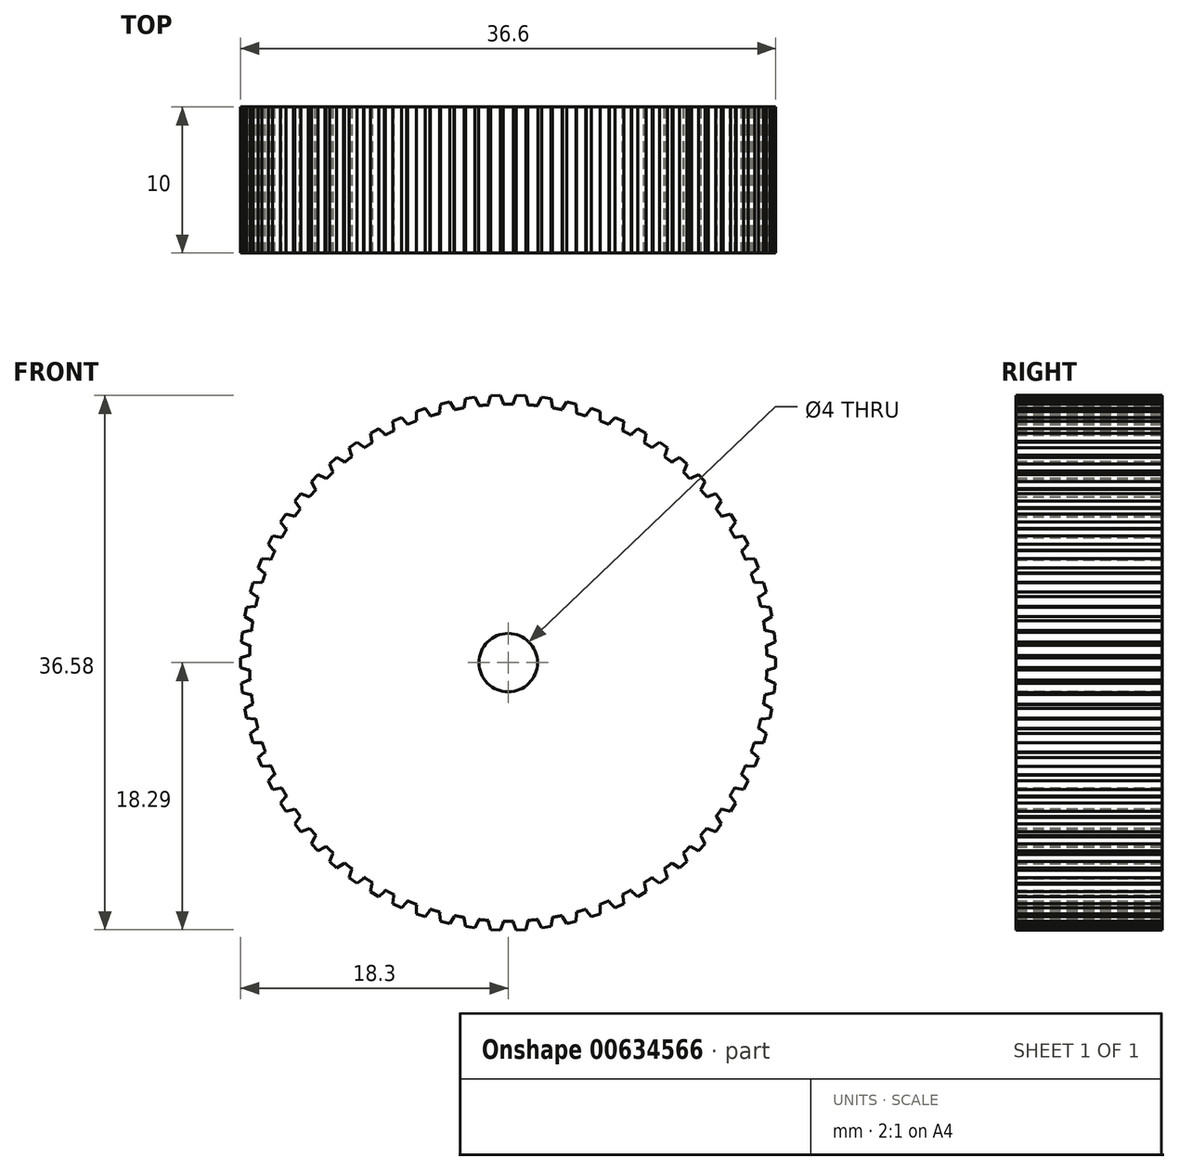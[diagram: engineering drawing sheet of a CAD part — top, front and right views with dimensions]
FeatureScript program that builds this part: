
annotation { "Feature Type Name" : "Feature", "Feature Type Description" : "" }
export const myFeature = defineFeature(function(context is Context, id is Id, definition is map)
    precondition{}
    {
        {
            var Q0;
            Q0=qCreatedBy(makeId("Front.planeOp"),FACE);
            var sketch = newSketch(context, id + "F0", { "sketchPlane" : qUnion([Q0])});
            skCircle(sketch, "E0", {"center": v(0, 0) * mm, "radius": 17.7 * mm});
            skLineSegment(sketch, "E1", {"start": v(0, 0) * mm, "end": v(17.7, 0) * mm, "construction": true});
            skLineSegment(sketch, "E2", {"start": v(17.7, 0) * mm, "end": v(18.3, 0) * mm, "construction": true});
            skLineSegment(sketch, "E3", {"start": v(18.3, 0) * mm, "end": v(18.3, 0.33) * mm});
            skLineSegment(sketch, "E4", {"start": v(17.7, 0.5) * mm, "end": v(17.8, 0.5) * mm});
            skLineSegment(sketch, "E5", {"start": v(17.8, 0.5) * mm, "end": v(18.3, 0.33) * mm});
            skLineSegment(sketch, "E6.MirrorCS", {"start": v(17.8, -0.5) * mm, "end": v(18.3, -0.33) * mm});
            skLineSegment(sketch, "E7.MirrorCS", {"start": v(18.3, 0) * mm, "end": v(18.3, -0.33) * mm});
            skLineSegment(sketch, "E8.MirrorCS", {"start": v(17.7, -0.5) * mm, "end": v(17.8, -0.5) * mm});
            skLineSegment(sketch, "E9.1.0", {"start": v(-28.82, -3.03) * mm, "end": v(-28.73, -3) * mm});
            skLineSegment(sketch, "E9.1.1", {"start": v(-28.73, -3) * mm, "end": v(-28.2, -3.01) * mm});
            skLineSegment(sketch, "E9.1.2", {"start": v(-28.1, -3.33) * mm, "end": v(-28.2, -3.01) * mm});
            skLineSegment(sketch, "E9.1.3", {"start": v(-28.1, -3.33) * mm, "end": v(-28, -3.64) * mm});
            skLineSegment(sketch, "E9.1.4", {"start": v(-28.43, -3.96) * mm, "end": v(-28, -3.64) * mm});
            skLineSegment(sketch, "E9.1.5", {"start": v(-28.53, -3.99) * mm, "end": v(-28.43, -3.96) * mm});
            skLineSegment(sketch, "E9.2.0", {"start": v(-72.23, -20.11) * mm, "end": v(-72.15, -20.06) * mm});
            skLineSegment(sketch, "E9.2.1", {"start": v(-72.15, -20.06) * mm, "end": v(-71.63, -19.91) * mm});
            skLineSegment(sketch, "E9.2.2", {"start": v(-71.45, -20.19) * mm, "end": v(-71.63, -19.91) * mm});
            skLineSegment(sketch, "E9.2.3", {"start": v(-71.45, -20.19) * mm, "end": v(-71.26, -20.46) * mm});
            skLineSegment(sketch, "E9.2.4", {"start": v(-71.58, -20.88) * mm, "end": v(-71.26, -20.46) * mm});
            skLineSegment(sketch, "E9.2.5", {"start": v(-71.67, -20.94) * mm, "end": v(-71.58, -20.88) * mm});
            skLineSegment(sketch, "E9.3.0", {"start": v(-108.67, -49.23) * mm, "end": v(-108.6, -49.15) * mm});
            skLineSegment(sketch, "E9.3.1", {"start": v(-108.6, -49.15) * mm, "end": v(-108.16, -48.86) * mm});
            skLineSegment(sketch, "E9.3.2", {"start": v(-107.9, -49.07) * mm, "end": v(-108.16, -48.86) * mm});
            skLineSegment(sketch, "E9.3.3", {"start": v(-107.9, -49.07) * mm, "end": v(-107.64, -49.28) * mm});
            skLineSegment(sketch, "E9.3.4", {"start": v(-107.83, -49.78) * mm, "end": v(-107.64, -49.28) * mm});
            skLineSegment(sketch, "E9.3.5", {"start": v(-107.89, -49.86) * mm, "end": v(-107.83, -49.78) * mm});
            skLineSegment(sketch, "E9.4.0", {"start": v(-134.91, -87.8) * mm, "end": v(-134.88, -87.7) * mm});
            skLineSegment(sketch, "E9.4.1", {"start": v(-134.88, -87.7) * mm, "end": v(-134.53, -87.3) * mm});
            skLineSegment(sketch, "E9.4.2", {"start": v(-134.23, -87.42) * mm, "end": v(-134.53, -87.3) * mm});
            skLineSegment(sketch, "E9.4.3", {"start": v(-134.23, -87.42) * mm, "end": v(-133.92, -87.54) * mm});
            skLineSegment(sketch, "E9.4.4", {"start": v(-133.95, -88.07) * mm, "end": v(-133.92, -87.54) * mm});
            skLineSegment(sketch, "E9.4.5", {"start": v(-133.98, -88.17) * mm, "end": v(-133.95, -88.07) * mm});
            skLineSegment(sketch, "E9.5.0", {"start": v(-148.62, -132.39) * mm, "end": v(-148.61, -132.29) * mm});
            skLineSegment(sketch, "E9.5.1", {"start": v(-148.61, -132.29) * mm, "end": v(-148.4, -131.8) * mm});
            skLineSegment(sketch, "E9.5.2", {"start": v(-148.08, -131.82) * mm, "end": v(-148.4, -131.8) * mm});
            skLineSegment(sketch, "E9.5.3", {"start": v(-148.08, -131.82) * mm, "end": v(-147.75, -131.85) * mm});
            skLineSegment(sketch, "E9.5.4", {"start": v(-147.62, -132.36) * mm, "end": v(-147.75, -131.85) * mm});
            skLineSegment(sketch, "E9.5.5", {"start": v(-147.62, -132.46) * mm, "end": v(-147.62, -132.36) * mm});
            skLineSegment(sketch, "E9.6.0", {"start": v(-148.58, -179.04) * mm, "end": v(-148.6, -178.94) * mm});
            skLineSegment(sketch, "E9.6.1", {"start": v(-148.6, -178.94) * mm, "end": v(-148.54, -178.4) * mm});
            skLineSegment(sketch, "E9.6.2", {"start": v(-148.22, -178.33) * mm, "end": v(-148.54, -178.4) * mm});
            skLineSegment(sketch, "E9.6.3", {"start": v(-148.22, -178.33) * mm, "end": v(-147.9, -178.26) * mm});
            skLineSegment(sketch, "E9.6.4", {"start": v(-147.62, -178.72) * mm, "end": v(-147.9, -178.26) * mm});
            skLineSegment(sketch, "E9.6.5", {"start": v(-147.6, -178.81) * mm, "end": v(-147.62, -178.72) * mm});
            skLineSegment(sketch, "E9.7.0", {"start": v(-134.78, -223.6) * mm, "end": v(-134.83, -223.51) * mm});
            skLineSegment(sketch, "E9.7.1", {"start": v(-134.83, -223.51) * mm, "end": v(-134.94, -222.99) * mm});
            skLineSegment(sketch, "E9.7.2", {"start": v(-134.65, -222.82) * mm, "end": v(-134.94, -222.99) * mm});
            skLineSegment(sketch, "E9.7.3", {"start": v(-134.65, -222.82) * mm, "end": v(-134.37, -222.66) * mm});
            skLineSegment(sketch, "E9.7.4", {"start": v(-133.97, -223.01) * mm, "end": v(-134.37, -222.66) * mm});
            skLineSegment(sketch, "E9.7.5", {"start": v(-133.92, -223.1) * mm, "end": v(-133.97, -223.01) * mm});
            skLineSegment(sketch, "E9.8.0", {"start": v(-108.47, -262.12) * mm, "end": v(-108.54, -262.05) * mm});
            skLineSegment(sketch, "E9.8.1", {"start": v(-108.54, -262.05) * mm, "end": v(-108.8, -261.58) * mm});
            skLineSegment(sketch, "E9.8.2", {"start": v(-108.57, -261.34) * mm, "end": v(-108.8, -261.58) * mm});
            skLineSegment(sketch, "E9.8.3", {"start": v(-108.57, -261.34) * mm, "end": v(-108.35, -261.1) * mm});
            skLineSegment(sketch, "E9.8.4", {"start": v(-107.86, -261.32) * mm, "end": v(-108.35, -261.1) * mm});
            skLineSegment(sketch, "E9.8.5", {"start": v(-107.79, -261.38) * mm, "end": v(-107.86, -261.32) * mm});
            skLineSegment(sketch, "E9.9.0", {"start": v(-71.97, -291.17) * mm, "end": v(-72.06, -291.12) * mm});
            skLineSegment(sketch, "E9.9.1", {"start": v(-72.06, -291.12) * mm, "end": v(-72.44, -290.75) * mm});
            skLineSegment(sketch, "E9.9.2", {"start": v(-72.3, -290.45) * mm, "end": v(-72.44, -290.75) * mm});
            skLineSegment(sketch, "E9.9.3", {"start": v(-72.3, -290.45) * mm, "end": v(-72.16, -290.16) * mm});
            skLineSegment(sketch, "E9.9.4", {"start": v(-71.63, -290.22) * mm, "end": v(-72.16, -290.16) * mm});
            skLineSegment(sketch, "E9.9.5", {"start": v(-71.54, -290.27) * mm, "end": v(-71.63, -290.22) * mm});
            skLineSegment(sketch, "E9.10.0", {"start": v(-28.53, -308.17) * mm, "end": v(-28.63, -308.15) * mm});
            skLineSegment(sketch, "E9.10.1", {"start": v(-28.63, -308.15) * mm, "end": v(-29.1, -307.9) * mm});
            skLineSegment(sketch, "E9.10.2", {"start": v(-29.06, -307.58) * mm, "end": v(-29.1, -307.9) * mm});
            skLineSegment(sketch, "E9.10.3", {"start": v(-29.06, -307.58) * mm, "end": v(-29, -307.26) * mm});
            skLineSegment(sketch, "E9.10.4", {"start": v(-28.48, -307.16) * mm, "end": v(-29, -307.26) * mm});
            skLineSegment(sketch, "E9.10.5", {"start": v(-28.38, -307.18) * mm, "end": v(-28.48, -307.16) * mm});
            skLineSegment(sketch, "E9.11.0", {"start": v(17.99, -311.6) * mm, "end": v(17.9, -311.62) * mm});
            skLineSegment(sketch, "E9.11.1", {"start": v(17.9, -311.62) * mm, "end": v(17.36, -311.53) * mm});
            skLineSegment(sketch, "E9.11.2", {"start": v(17.31, -311.2) * mm, "end": v(17.36, -311.53) * mm});
            skLineSegment(sketch, "E9.11.3", {"start": v(17.31, -311.2) * mm, "end": v(17.27, -310.88) * mm});
            skLineSegment(sketch, "E9.11.4", {"start": v(17.74, -310.64) * mm, "end": v(17.27, -310.88) * mm});
            skLineSegment(sketch, "E9.11.5", {"start": v(17.84, -310.62) * mm, "end": v(17.74, -310.64) * mm});
            skLineSegment(sketch, "E9.12.0", {"start": v(63.46, -301.19) * mm, "end": v(63.37, -301.23) * mm});
            skLineSegment(sketch, "E9.12.1", {"start": v(63.37, -301.23) * mm, "end": v(62.84, -301.3) * mm});
            skLineSegment(sketch, "E9.12.2", {"start": v(62.7, -301) * mm, "end": v(62.84, -301.3) * mm});
            skLineSegment(sketch, "E9.12.3", {"start": v(62.7, -301) * mm, "end": v(62.55, -300.7) * mm});
            skLineSegment(sketch, "E9.12.4", {"start": v(62.93, -300.33) * mm, "end": v(62.55, -300.7) * mm});
            skLineSegment(sketch, "E9.12.5", {"start": v(63.02, -300.28) * mm, "end": v(62.93, -300.33) * mm});
            skLineSegment(sketch, "E9.13.0", {"start": v(103.83, -277.82) * mm, "end": v(103.76, -277.9) * mm});
            skLineSegment(sketch, "E9.13.1", {"start": v(103.76, -277.9) * mm, "end": v(103.27, -278.11) * mm});
            skLineSegment(sketch, "E9.13.2", {"start": v(103.05, -277.87) * mm, "end": v(103.27, -278.11) * mm});
            skLineSegment(sketch, "E9.13.3", {"start": v(103.05, -277.87) * mm, "end": v(102.82, -277.63) * mm});
            skLineSegment(sketch, "E9.13.4", {"start": v(103.08, -277.16) * mm, "end": v(102.82, -277.63) * mm});
            skLineSegment(sketch, "E9.13.5", {"start": v(103.15, -277.1) * mm, "end": v(103.08, -277.16) * mm});
            skLineSegment(sketch, "E9.14.0", {"start": v(135.53, -243.6) * mm, "end": v(135.48, -243.68) * mm});
            skLineSegment(sketch, "E9.14.1", {"start": v(135.48, -243.68) * mm, "end": v(135.08, -244.04) * mm});
            skLineSegment(sketch, "E9.14.2", {"start": v(134.8, -243.87) * mm, "end": v(135.08, -244.04) * mm});
            skLineSegment(sketch, "E9.14.3", {"start": v(134.8, -243.87) * mm, "end": v(134.5, -243.7) * mm});
            skLineSegment(sketch, "E9.14.4", {"start": v(134.61, -243.18) * mm, "end": v(134.5, -243.7) * mm});
            skLineSegment(sketch, "E9.14.5", {"start": v(134.66, -243.1) * mm, "end": v(134.61, -243.18) * mm});
            skLineSegment(sketch, "E9.15.0", {"start": v(155.73, -201.55) * mm, "end": v(155.7, -201.65) * mm});
            skLineSegment(sketch, "E9.15.1", {"start": v(155.7, -201.65) * mm, "end": v(155.43, -202.1) * mm});
            skLineSegment(sketch, "E9.15.2", {"start": v(155.1, -202.03) * mm, "end": v(155.43, -202.1) * mm});
            skLineSegment(sketch, "E9.15.3", {"start": v(155.1, -202.03) * mm, "end": v(154.79, -201.96) * mm});
            skLineSegment(sketch, "E9.15.4", {"start": v(154.73, -201.43) * mm, "end": v(154.79, -201.96) * mm});
            skLineSegment(sketch, "E9.15.5", {"start": v(154.76, -201.33) * mm, "end": v(154.73, -201.43) * mm});
            skLineSegment(sketch, "E9.16.0", {"start": v(162.64, -155.42) * mm, "end": v(162.65, -155.52) * mm});
            skLineSegment(sketch, "E9.16.1", {"start": v(162.65, -155.52) * mm, "end": v(162.51, -156.04) * mm});
            skLineSegment(sketch, "E9.16.2", {"start": v(162.19, -156.06) * mm, "end": v(162.51, -156.04) * mm});
            skLineSegment(sketch, "E9.16.3", {"start": v(162.19, -156.06) * mm, "end": v(161.86, -156.08) * mm});
            skLineSegment(sketch, "E9.16.4", {"start": v(161.65, -155.6) * mm, "end": v(161.86, -156.08) * mm});
            skLineSegment(sketch, "E9.16.5", {"start": v(161.64, -155.5) * mm, "end": v(161.65, -155.6) * mm});
            skLineSegment(sketch, "E9.17.0", {"start": v(155.64, -109.3) * mm, "end": v(155.68, -109.39) * mm});
            skLineSegment(sketch, "E9.17.1", {"start": v(155.68, -109.39) * mm, "end": v(155.7, -109.92) * mm});
            skLineSegment(sketch, "E9.17.2", {"start": v(155.4, -110.04) * mm, "end": v(155.7, -109.92) * mm});
            skLineSegment(sketch, "E9.17.3", {"start": v(155.4, -110.04) * mm, "end": v(155.1, -110.17) * mm});
            skLineSegment(sketch, "E9.17.4", {"start": v(154.75, -109.76) * mm, "end": v(155.1, -110.17) * mm});
            skLineSegment(sketch, "E9.17.5", {"start": v(154.71, -109.66) * mm, "end": v(154.75, -109.76) * mm});
            skLineSegment(sketch, "E9.18.0", {"start": v(135.36, -67.29) * mm, "end": v(135.43, -67.37) * mm});
            skLineSegment(sketch, "E9.18.1", {"start": v(135.43, -67.37) * mm, "end": v(135.6, -67.87) * mm});
            skLineSegment(sketch, "E9.18.2", {"start": v(135.35, -68.07) * mm, "end": v(135.6, -67.87) * mm});
            skLineSegment(sketch, "E9.18.3", {"start": v(135.35, -68.07) * mm, "end": v(135.1, -68.28) * mm});
            skLineSegment(sketch, "E9.18.4", {"start": v(134.64, -67.99) * mm, "end": v(135.1, -68.28) * mm});
            skLineSegment(sketch, "E9.18.5", {"start": v(134.58, -67.91) * mm, "end": v(134.64, -67.99) * mm});
            skLineSegment(sketch, "E9.19.0", {"start": v(103.6, -33.12) * mm, "end": v(103.68, -33.18) * mm});
            skLineSegment(sketch, "E9.19.1", {"start": v(103.68, -33.18) * mm, "end": v(104, -33.6) * mm});
            skLineSegment(sketch, "E9.19.2", {"start": v(103.82, -33.88) * mm, "end": v(104, -33.6) * mm});
            skLineSegment(sketch, "E9.19.3", {"start": v(103.82, -33.88) * mm, "end": v(103.64, -34.15) * mm});
            skLineSegment(sketch, "E9.19.4", {"start": v(103.12, -34) * mm, "end": v(103.64, -34.15) * mm});
            skLineSegment(sketch, "E9.19.5", {"start": v(103.04, -33.95) * mm, "end": v(103.12, -34) * mm});
            skLineSegment(sketch, "E9.20.0", {"start": v(63.18, -9.84) * mm, "end": v(63.28, -9.87) * mm});
            skLineSegment(sketch, "E9.20.1", {"start": v(63.28, -9.87) * mm, "end": v(63.71, -10.18) * mm});
            skLineSegment(sketch, "E9.20.2", {"start": v(63.61, -10.5) * mm, "end": v(63.71, -10.18) * mm});
            skLineSegment(sketch, "E9.20.3", {"start": v(63.61, -10.5) * mm, "end": v(63.52, -10.8) * mm});
            skLineSegment(sketch, "E9.20.4", {"start": v(62.98, -10.82) * mm, "end": v(63.52, -10.8) * mm});
            skLineSegment(sketch, "E9.20.5", {"start": v(62.89, -10.8) * mm, "end": v(62.98, -10.82) * mm});
            skLineSegment(sketch, "E10.1.0", {"start": v(17.57, 2.18) * mm, "end": v(17.66, 2.19) * mm});
            skLineSegment(sketch, "E10.1.1", {"start": v(17.66, 2.19) * mm, "end": v(18.19, 2.07) * mm});
            skLineSegment(sketch, "E10.1.2", {"start": v(18.22, 1.74) * mm, "end": v(18.25, 1.41) * mm});
            skLineSegment(sketch, "E10.1.3", {"start": v(18.22, 1.74) * mm, "end": v(18.19, 2.07) * mm});
            skLineSegment(sketch, "E10.1.4", {"start": v(17.76, 1.2) * mm, "end": v(18.25, 1.41) * mm});
            skLineSegment(sketch, "E10.1.5", {"start": v(17.66, 1.18) * mm, "end": v(17.76, 1.2) * mm});
            skLineSegment(sketch, "E10.2.0", {"start": v(17.28, 3.84) * mm, "end": v(17.38, 3.86) * mm});
            skLineSegment(sketch, "E10.2.1", {"start": v(17.38, 3.86) * mm, "end": v(17.9, 3.79) * mm});
            skLineSegment(sketch, "E10.2.2", {"start": v(17.97, 3.46) * mm, "end": v(18.03, 3.14) * mm});
            skLineSegment(sketch, "E10.2.3", {"start": v(17.97, 3.46) * mm, "end": v(17.9, 3.79) * mm});
            skLineSegment(sketch, "E10.2.4", {"start": v(17.57, 2.88) * mm, "end": v(18.03, 3.14) * mm});
            skLineSegment(sketch, "E10.2.5", {"start": v(17.47, 2.86) * mm, "end": v(17.57, 2.88) * mm});
            skLineSegment(sketch, "E10.3.0", {"start": v(16.84, 5.46) * mm, "end": v(16.93, 5.5) * mm});
            skLineSegment(sketch, "E10.3.1", {"start": v(16.93, 5.5) * mm, "end": v(17.47, 5.47) * mm});
            skLineSegment(sketch, "E10.3.2", {"start": v(17.56, 5.16) * mm, "end": v(17.65, 4.84) * mm});
            skLineSegment(sketch, "E10.3.3", {"start": v(17.56, 5.16) * mm, "end": v(17.47, 5.47) * mm});
            skLineSegment(sketch, "E10.3.4", {"start": v(17.21, 4.53) * mm, "end": v(17.65, 4.84) * mm});
            skLineSegment(sketch, "E10.3.5", {"start": v(17.12, 4.5) * mm, "end": v(17.21, 4.53) * mm});
            skLineSegment(sketch, "E10.4.0", {"start": v(16.24, 7.04) * mm, "end": v(16.33, 7.08) * mm});
            skLineSegment(sketch, "E10.4.1", {"start": v(16.33, 7.08) * mm, "end": v(16.87, 7.1) * mm});
            skLineSegment(sketch, "E10.4.2", {"start": v(16.99, 6.8) * mm, "end": v(17.11, 6.5) * mm});
            skLineSegment(sketch, "E10.4.3", {"start": v(16.99, 6.8) * mm, "end": v(16.87, 7.1) * mm});
            skLineSegment(sketch, "E10.4.4", {"start": v(16.7, 6.15) * mm, "end": v(17.11, 6.5) * mm});
            skLineSegment(sketch, "E10.4.5", {"start": v(16.61, 6.11) * mm, "end": v(16.7, 6.15) * mm});
            skLineSegment(sketch, "E10.5.0", {"start": v(15.5, 8.55) * mm, "end": v(15.59, 8.6) * mm});
            skLineSegment(sketch, "E10.5.1", {"start": v(15.59, 8.6) * mm, "end": v(16.11, 8.68) * mm});
            skLineSegment(sketch, "E10.5.2", {"start": v(16.27, 8.39) * mm, "end": v(16.42, 8.1) * mm});
            skLineSegment(sketch, "E10.5.3", {"start": v(16.27, 8.39) * mm, "end": v(16.11, 8.68) * mm});
            skLineSegment(sketch, "E10.5.4", {"start": v(16.04, 7.7) * mm, "end": v(16.42, 8.1) * mm});
            skLineSegment(sketch, "E10.5.5", {"start": v(15.96, 7.66) * mm, "end": v(16.04, 7.7) * mm});
            skLineSegment(sketch, "E10.6.0", {"start": v(14.61, 9.99) * mm, "end": v(14.7, 10.04) * mm});
            skLineSegment(sketch, "E10.6.1", {"start": v(14.7, 10.04) * mm, "end": v(15.22, 10.17) * mm});
            skLineSegment(sketch, "E10.6.2", {"start": v(15.4, 9.9) * mm, "end": v(15.57, 9.62) * mm});
            skLineSegment(sketch, "E10.6.3", {"start": v(15.4, 9.9) * mm, "end": v(15.22, 10.17) * mm});
            skLineSegment(sketch, "E10.6.4", {"start": v(15.24, 9.2) * mm, "end": v(15.57, 9.62) * mm});
            skLineSegment(sketch, "E10.6.5", {"start": v(15.15, 9.14) * mm, "end": v(15.24, 9.2) * mm});
            skLineSegment(sketch, "E10.7.0", {"start": v(13.6, 11.33) * mm, "end": v(13.68, 11.4) * mm});
            skLineSegment(sketch, "E10.7.1", {"start": v(13.68, 11.4) * mm, "end": v(14.18, 11.57) * mm});
            skLineSegment(sketch, "E10.7.2", {"start": v(14.38, 11.31) * mm, "end": v(14.59, 11.05) * mm});
            skLineSegment(sketch, "E10.7.3", {"start": v(14.38, 11.31) * mm, "end": v(14.18, 11.57) * mm});
            skLineSegment(sketch, "E10.7.4", {"start": v(14.3, 10.6) * mm, "end": v(14.59, 11.05) * mm});
            skLineSegment(sketch, "E10.7.5", {"start": v(14.22, 10.54) * mm, "end": v(14.3, 10.6) * mm});
            skLineSegment(sketch, "E10.8.0", {"start": v(12.46, 12.57) * mm, "end": v(12.53, 12.64) * mm});
            skLineSegment(sketch, "E10.8.1", {"start": v(12.53, 12.64) * mm, "end": v(13.02, 12.87) * mm});
            skLineSegment(sketch, "E10.8.2", {"start": v(13.24, 12.63) * mm, "end": v(13.47, 12.39) * mm});
            skLineSegment(sketch, "E10.8.3", {"start": v(13.24, 12.63) * mm, "end": v(13.02, 12.87) * mm});
            skLineSegment(sketch, "E10.8.4", {"start": v(13.22, 11.92) * mm, "end": v(13.47, 12.39) * mm});
            skLineSegment(sketch, "E10.8.5", {"start": v(13.15, 11.85) * mm, "end": v(13.22, 11.92) * mm});
            skLineSegment(sketch, "E10.9.0", {"start": v(11.2, 13.7) * mm, "end": v(11.27, 13.77) * mm});
            skLineSegment(sketch, "E10.9.1", {"start": v(11.27, 13.77) * mm, "end": v(11.73, 14.05) * mm});
            skLineSegment(sketch, "E10.9.2", {"start": v(11.98, 13.83) * mm, "end": v(12.23, 13.61) * mm});
            skLineSegment(sketch, "E10.9.3", {"start": v(11.98, 13.83) * mm, "end": v(11.73, 14.05) * mm});
            skLineSegment(sketch, "E10.9.4", {"start": v(12.03, 13.12) * mm, "end": v(12.23, 13.61) * mm});
            skLineSegment(sketch, "E10.9.5", {"start": v(11.96, 13.04) * mm, "end": v(12.03, 13.12) * mm});
            skLineSegment(sketch, "E10.10.0", {"start": v(9.86, 14.7) * mm, "end": v(9.91, 14.78) * mm});
            skLineSegment(sketch, "E10.10.1", {"start": v(9.91, 14.78) * mm, "end": v(10.35, 15.1) * mm});
            skLineSegment(sketch, "E10.10.2", {"start": v(10.62, 14.9) * mm, "end": v(10.88, 14.72) * mm});
            skLineSegment(sketch, "E10.10.3", {"start": v(10.62, 14.9) * mm, "end": v(10.35, 15.1) * mm});
            skLineSegment(sketch, "E10.10.4", {"start": v(10.73, 14.2) * mm, "end": v(10.88, 14.72) * mm});
            skLineSegment(sketch, "E10.10.5", {"start": v(10.67, 14.12) * mm, "end": v(10.73, 14.2) * mm});
            skLineSegment(sketch, "E10.11.0", {"start": v(8.41, 15.57) * mm, "end": v(8.46, 15.66) * mm});
            skLineSegment(sketch, "E10.11.1", {"start": v(8.46, 15.66) * mm, "end": v(8.86, 16.01) * mm});
            skLineSegment(sketch, "E10.11.2", {"start": v(9.15, 15.85) * mm, "end": v(9.44, 15.68) * mm});
            skLineSegment(sketch, "E10.11.3", {"start": v(9.15, 15.85) * mm, "end": v(8.86, 16.01) * mm});
            skLineSegment(sketch, "E10.11.4", {"start": v(9.33, 15.16) * mm, "end": v(9.44, 15.68) * mm});
            skLineSegment(sketch, "E10.11.5", {"start": v(9.28, 15.07) * mm, "end": v(9.33, 15.16) * mm});
            skLineSegment(sketch, "E10.12.0", {"start": v(6.9, 16.3) * mm, "end": v(6.94, 16.4) * mm});
            skLineSegment(sketch, "E10.12.1", {"start": v(6.94, 16.4) * mm, "end": v(7.3, 16.78) * mm});
            skLineSegment(sketch, "E10.12.2", {"start": v(7.6, 16.65) * mm, "end": v(7.9, 16.5) * mm});
            skLineSegment(sketch, "E10.12.3", {"start": v(7.6, 16.65) * mm, "end": v(7.3, 16.78) * mm});
            skLineSegment(sketch, "E10.12.4", {"start": v(7.85, 15.98) * mm, "end": v(7.9, 16.5) * mm});
            skLineSegment(sketch, "E10.12.5", {"start": v(7.8, 15.89) * mm, "end": v(7.85, 15.98) * mm});
            skLineSegment(sketch, "E10.13.0", {"start": v(5.31, 16.88) * mm, "end": v(5.35, 16.98) * mm});
            skLineSegment(sketch, "E10.13.1", {"start": v(5.35, 16.98) * mm, "end": v(5.67, 17.4) * mm});
            skLineSegment(sketch, "E10.13.2", {"start": v(5.99, 17.3) * mm, "end": v(6.3, 17.19) * mm});
            skLineSegment(sketch, "E10.13.3", {"start": v(5.99, 17.3) * mm, "end": v(5.67, 17.4) * mm});
            skLineSegment(sketch, "E10.13.4", {"start": v(6.3, 16.65) * mm, "end": v(6.3, 17.19) * mm});
            skLineSegment(sketch, "E10.13.5", {"start": v(6.26, 16.56) * mm, "end": v(6.3, 16.65) * mm});
            skLineSegment(sketch, "E10.14.0", {"start": v(3.69, 17.31) * mm, "end": v(3.7, 17.4) * mm});
            skLineSegment(sketch, "E10.14.1", {"start": v(3.7, 17.4) * mm, "end": v(4, 17.86) * mm});
            skLineSegment(sketch, "E10.14.2", {"start": v(4.31, 17.78) * mm, "end": v(4.64, 17.7) * mm});
            skLineSegment(sketch, "E10.14.3", {"start": v(4.31, 17.78) * mm, "end": v(4, 17.86) * mm});
            skLineSegment(sketch, "E10.14.4", {"start": v(4.68, 17.17) * mm, "end": v(4.64, 17.7) * mm});
            skLineSegment(sketch, "E10.14.5", {"start": v(4.66, 17.08) * mm, "end": v(4.68, 17.17) * mm});
            skLineSegment(sketch, "E10.15.0", {"start": v(2.02, 17.58) * mm, "end": v(2.04, 17.68) * mm});
            skLineSegment(sketch, "E10.15.1", {"start": v(2.04, 17.68) * mm, "end": v(2.28, 18.16) * mm});
            skLineSegment(sketch, "E10.15.2", {"start": v(2.6, 18.11) * mm, "end": v(2.93, 18.07) * mm});
            skLineSegment(sketch, "E10.15.3", {"start": v(2.6, 18.11) * mm, "end": v(2.28, 18.16) * mm});
            skLineSegment(sketch, "E10.15.4", {"start": v(3.03, 17.54) * mm, "end": v(2.93, 18.07) * mm});
            skLineSegment(sketch, "E10.15.5", {"start": v(3.01, 17.44) * mm, "end": v(3.03, 17.54) * mm});
            skLineSegment(sketch, "E10.16.0", {"start": v(0.34, 17.7) * mm, "end": v(0.35, 17.8) * mm});
            skLineSegment(sketch, "E10.16.1", {"start": v(0.35, 17.8) * mm, "end": v(0.54, 18.3) * mm});
            skLineSegment(sketch, "E10.16.2", {"start": v(0.87, 18.28) * mm, "end": v(1.2, 18.26) * mm});
            skLineSegment(sketch, "E10.16.3", {"start": v(0.87, 18.28) * mm, "end": v(0.54, 18.3) * mm});
            skLineSegment(sketch, "E10.16.4", {"start": v(1.35, 17.75) * mm, "end": v(1.2, 18.26) * mm});
            skLineSegment(sketch, "E10.16.5", {"start": v(1.34, 17.65) * mm, "end": v(1.35, 17.75) * mm});
            skLineSegment(sketch, "E10.17.0", {"start": v(-1.34, 17.65) * mm, "end": v(-1.35, 17.75) * mm});
            skLineSegment(sketch, "E10.17.1", {"start": v(-1.35, 17.75) * mm, "end": v(-1.2, 18.26) * mm});
            skLineSegment(sketch, "E10.17.2", {"start": v(-0.87, 18.28) * mm, "end": v(-0.54, 18.3) * mm});
            skLineSegment(sketch, "E10.17.3", {"start": v(-0.87, 18.28) * mm, "end": v(-1.2, 18.26) * mm});
            skLineSegment(sketch, "E10.17.4", {"start": v(-0.35, 17.8) * mm, "end": v(-0.54, 18.3) * mm});
            skLineSegment(sketch, "E10.17.5", {"start": v(-0.34, 17.7) * mm, "end": v(-0.35, 17.8) * mm});
            skLineSegment(sketch, "E10.18.0", {"start": v(-3.01, 17.44) * mm, "end": v(-3.03, 17.54) * mm});
            skLineSegment(sketch, "E10.18.1", {"start": v(-3.03, 17.54) * mm, "end": v(-2.93, 18.07) * mm});
            skLineSegment(sketch, "E10.18.2", {"start": v(-2.6, 18.11) * mm, "end": v(-2.28, 18.16) * mm});
            skLineSegment(sketch, "E10.18.3", {"start": v(-2.6, 18.11) * mm, "end": v(-2.93, 18.07) * mm});
            skLineSegment(sketch, "E10.18.4", {"start": v(-2.04, 17.68) * mm, "end": v(-2.28, 18.16) * mm});
            skLineSegment(sketch, "E10.18.5", {"start": v(-2.02, 17.58) * mm, "end": v(-2.04, 17.68) * mm});
            skLineSegment(sketch, "E10.19.0", {"start": v(-4.66, 17.08) * mm, "end": v(-4.68, 17.17) * mm});
            skLineSegment(sketch, "E10.19.1", {"start": v(-4.68, 17.17) * mm, "end": v(-4.64, 17.7) * mm});
            skLineSegment(sketch, "E10.19.2", {"start": v(-4.31, 17.78) * mm, "end": v(-4, 17.86) * mm});
            skLineSegment(sketch, "E10.19.3", {"start": v(-4.31, 17.78) * mm, "end": v(-4.64, 17.7) * mm});
            skLineSegment(sketch, "E10.19.4", {"start": v(-3.7, 17.4) * mm, "end": v(-4, 17.86) * mm});
            skLineSegment(sketch, "E10.19.5", {"start": v(-3.69, 17.31) * mm, "end": v(-3.7, 17.4) * mm});
            skLineSegment(sketch, "E10.20.0", {"start": v(-6.26, 16.56) * mm, "end": v(-6.3, 16.65) * mm});
            skLineSegment(sketch, "E10.20.1", {"start": v(-6.3, 16.65) * mm, "end": v(-6.3, 17.19) * mm});
            skLineSegment(sketch, "E10.20.2", {"start": v(-5.99, 17.3) * mm, "end": v(-5.67, 17.4) * mm});
            skLineSegment(sketch, "E10.20.3", {"start": v(-5.99, 17.3) * mm, "end": v(-6.3, 17.19) * mm});
            skLineSegment(sketch, "E10.20.4", {"start": v(-5.35, 16.98) * mm, "end": v(-5.67, 17.4) * mm});
            skLineSegment(sketch, "E10.20.5", {"start": v(-5.31, 16.88) * mm, "end": v(-5.35, 16.98) * mm});
            skLineSegment(sketch, "E10.21.0", {"start": v(-7.8, 15.89) * mm, "end": v(-7.85, 15.98) * mm});
            skLineSegment(sketch, "E10.21.1", {"start": v(-7.85, 15.98) * mm, "end": v(-7.9, 16.5) * mm});
            skLineSegment(sketch, "E10.21.2", {"start": v(-7.6, 16.65) * mm, "end": v(-7.3, 16.78) * mm});
            skLineSegment(sketch, "E10.21.3", {"start": v(-7.6, 16.65) * mm, "end": v(-7.9, 16.5) * mm});
            skLineSegment(sketch, "E10.21.4", {"start": v(-6.94, 16.4) * mm, "end": v(-7.3, 16.78) * mm});
            skLineSegment(sketch, "E10.21.5", {"start": v(-6.9, 16.3) * mm, "end": v(-6.94, 16.4) * mm});
            skLineSegment(sketch, "E10.22.0", {"start": v(-9.28, 15.07) * mm, "end": v(-9.33, 15.16) * mm});
            skLineSegment(sketch, "E10.22.1", {"start": v(-9.33, 15.16) * mm, "end": v(-9.44, 15.68) * mm});
            skLineSegment(sketch, "E10.22.2", {"start": v(-9.15, 15.85) * mm, "end": v(-8.86, 16.01) * mm});
            skLineSegment(sketch, "E10.22.3", {"start": v(-9.15, 15.85) * mm, "end": v(-9.44, 15.68) * mm});
            skLineSegment(sketch, "E10.22.4", {"start": v(-8.46, 15.66) * mm, "end": v(-8.86, 16.01) * mm});
            skLineSegment(sketch, "E10.22.5", {"start": v(-8.41, 15.57) * mm, "end": v(-8.46, 15.66) * mm});
            skLineSegment(sketch, "E10.23.0", {"start": v(-10.67, 14.12) * mm, "end": v(-10.73, 14.2) * mm});
            skLineSegment(sketch, "E10.23.1", {"start": v(-10.73, 14.2) * mm, "end": v(-10.88, 14.72) * mm});
            skLineSegment(sketch, "E10.23.2", {"start": v(-10.62, 14.9) * mm, "end": v(-10.35, 15.1) * mm});
            skLineSegment(sketch, "E10.23.3", {"start": v(-10.62, 14.9) * mm, "end": v(-10.88, 14.72) * mm});
            skLineSegment(sketch, "E10.23.4", {"start": v(-9.91, 14.78) * mm, "end": v(-10.35, 15.1) * mm});
            skLineSegment(sketch, "E10.23.5", {"start": v(-9.86, 14.7) * mm, "end": v(-9.91, 14.78) * mm});
            skLineSegment(sketch, "E10.24.0", {"start": v(-11.96, 13.04) * mm, "end": v(-12.03, 13.12) * mm});
            skLineSegment(sketch, "E10.24.1", {"start": v(-12.03, 13.12) * mm, "end": v(-12.23, 13.61) * mm});
            skLineSegment(sketch, "E10.24.2", {"start": v(-11.98, 13.83) * mm, "end": v(-11.73, 14.05) * mm});
            skLineSegment(sketch, "E10.24.3", {"start": v(-11.98, 13.83) * mm, "end": v(-12.23, 13.61) * mm});
            skLineSegment(sketch, "E10.24.4", {"start": v(-11.27, 13.77) * mm, "end": v(-11.73, 14.05) * mm});
            skLineSegment(sketch, "E10.24.5", {"start": v(-11.2, 13.7) * mm, "end": v(-11.27, 13.77) * mm});
            skLineSegment(sketch, "E10.25.0", {"start": v(-13.15, 11.85) * mm, "end": v(-13.22, 11.92) * mm});
            skLineSegment(sketch, "E10.25.1", {"start": v(-13.22, 11.92) * mm, "end": v(-13.47, 12.39) * mm});
            skLineSegment(sketch, "E10.25.2", {"start": v(-13.24, 12.63) * mm, "end": v(-13.02, 12.87) * mm});
            skLineSegment(sketch, "E10.25.3", {"start": v(-13.24, 12.63) * mm, "end": v(-13.47, 12.39) * mm});
            skLineSegment(sketch, "E10.25.4", {"start": v(-12.53, 12.64) * mm, "end": v(-13.02, 12.87) * mm});
            skLineSegment(sketch, "E10.25.5", {"start": v(-12.46, 12.57) * mm, "end": v(-12.53, 12.64) * mm});
            skLineSegment(sketch, "E10.26.0", {"start": v(-14.22, 10.54) * mm, "end": v(-14.3, 10.6) * mm});
            skLineSegment(sketch, "E10.26.1", {"start": v(-14.3, 10.6) * mm, "end": v(-14.59, 11.05) * mm});
            skLineSegment(sketch, "E10.26.2", {"start": v(-14.38, 11.31) * mm, "end": v(-14.18, 11.57) * mm});
            skLineSegment(sketch, "E10.26.3", {"start": v(-14.38, 11.31) * mm, "end": v(-14.59, 11.05) * mm});
            skLineSegment(sketch, "E10.26.4", {"start": v(-13.68, 11.4) * mm, "end": v(-14.18, 11.57) * mm});
            skLineSegment(sketch, "E10.26.5", {"start": v(-13.6, 11.33) * mm, "end": v(-13.68, 11.4) * mm});
            skLineSegment(sketch, "E10.27.0", {"start": v(-15.15, 9.14) * mm, "end": v(-15.24, 9.2) * mm});
            skLineSegment(sketch, "E10.27.1", {"start": v(-15.24, 9.2) * mm, "end": v(-15.57, 9.62) * mm});
            skLineSegment(sketch, "E10.27.2", {"start": v(-15.4, 9.9) * mm, "end": v(-15.22, 10.17) * mm});
            skLineSegment(sketch, "E10.27.3", {"start": v(-15.4, 9.9) * mm, "end": v(-15.57, 9.62) * mm});
            skLineSegment(sketch, "E10.27.4", {"start": v(-14.7, 10.04) * mm, "end": v(-15.22, 10.17) * mm});
            skLineSegment(sketch, "E10.27.5", {"start": v(-14.61, 9.99) * mm, "end": v(-14.7, 10.04) * mm});
            skLineSegment(sketch, "E10.28.0", {"start": v(-15.96, 7.66) * mm, "end": v(-16.04, 7.7) * mm});
            skLineSegment(sketch, "E10.28.1", {"start": v(-16.04, 7.7) * mm, "end": v(-16.42, 8.1) * mm});
            skLineSegment(sketch, "E10.28.2", {"start": v(-16.27, 8.39) * mm, "end": v(-16.11, 8.68) * mm});
            skLineSegment(sketch, "E10.28.3", {"start": v(-16.27, 8.39) * mm, "end": v(-16.42, 8.1) * mm});
            skLineSegment(sketch, "E10.28.4", {"start": v(-15.59, 8.6) * mm, "end": v(-16.11, 8.68) * mm});
            skLineSegment(sketch, "E10.28.5", {"start": v(-15.5, 8.55) * mm, "end": v(-15.59, 8.6) * mm});
            skLineSegment(sketch, "E10.29.0", {"start": v(-16.61, 6.11) * mm, "end": v(-16.7, 6.15) * mm});
            skLineSegment(sketch, "E10.29.1", {"start": v(-16.7, 6.15) * mm, "end": v(-17.11, 6.5) * mm});
            skLineSegment(sketch, "E10.29.2", {"start": v(-16.99, 6.8) * mm, "end": v(-16.87, 7.1) * mm});
            skLineSegment(sketch, "E10.29.3", {"start": v(-16.99, 6.8) * mm, "end": v(-17.11, 6.5) * mm});
            skLineSegment(sketch, "E10.29.4", {"start": v(-16.33, 7.08) * mm, "end": v(-16.87, 7.1) * mm});
            skLineSegment(sketch, "E10.29.5", {"start": v(-16.24, 7.04) * mm, "end": v(-16.33, 7.08) * mm});
            skLineSegment(sketch, "E10.30.0", {"start": v(-17.12, 4.5) * mm, "end": v(-17.21, 4.53) * mm});
            skLineSegment(sketch, "E10.30.1", {"start": v(-17.21, 4.53) * mm, "end": v(-17.65, 4.84) * mm});
            skLineSegment(sketch, "E10.30.2", {"start": v(-17.56, 5.16) * mm, "end": v(-17.47, 5.47) * mm});
            skLineSegment(sketch, "E10.30.3", {"start": v(-17.56, 5.16) * mm, "end": v(-17.65, 4.84) * mm});
            skLineSegment(sketch, "E10.30.4", {"start": v(-16.93, 5.5) * mm, "end": v(-17.47, 5.47) * mm});
            skLineSegment(sketch, "E10.30.5", {"start": v(-16.84, 5.46) * mm, "end": v(-16.93, 5.5) * mm});
            skLineSegment(sketch, "E10.31.0", {"start": v(-17.47, 2.86) * mm, "end": v(-17.57, 2.88) * mm});
            skLineSegment(sketch, "E10.31.1", {"start": v(-17.57, 2.88) * mm, "end": v(-18.03, 3.14) * mm});
            skLineSegment(sketch, "E10.31.2", {"start": v(-17.97, 3.46) * mm, "end": v(-17.9, 3.79) * mm});
            skLineSegment(sketch, "E10.31.3", {"start": v(-17.97, 3.46) * mm, "end": v(-18.03, 3.14) * mm});
            skLineSegment(sketch, "E10.31.4", {"start": v(-17.38, 3.86) * mm, "end": v(-17.9, 3.79) * mm});
            skLineSegment(sketch, "E10.31.5", {"start": v(-17.28, 3.84) * mm, "end": v(-17.38, 3.86) * mm});
            skLineSegment(sketch, "E10.32.0", {"start": v(-17.66, 1.18) * mm, "end": v(-17.76, 1.2) * mm});
            skLineSegment(sketch, "E10.32.1", {"start": v(-17.76, 1.2) * mm, "end": v(-18.25, 1.41) * mm});
            skLineSegment(sketch, "E10.32.2", {"start": v(-18.22, 1.74) * mm, "end": v(-18.19, 2.07) * mm});
            skLineSegment(sketch, "E10.32.3", {"start": v(-18.22, 1.74) * mm, "end": v(-18.25, 1.41) * mm});
            skLineSegment(sketch, "E10.32.4", {"start": v(-17.66, 2.19) * mm, "end": v(-18.19, 2.07) * mm});
            skLineSegment(sketch, "E10.32.5", {"start": v(-17.57, 2.18) * mm, "end": v(-17.66, 2.19) * mm});
            skLineSegment(sketch, "E10.33.0", {"start": v(-17.7, -0.5) * mm, "end": v(-17.8, -0.5) * mm});
            skLineSegment(sketch, "E10.33.1", {"start": v(-17.8, -0.5) * mm, "end": v(-18.3, -0.33) * mm});
            skLineSegment(sketch, "E10.33.2", {"start": v(-18.3, 0) * mm, "end": v(-18.3, 0.33) * mm});
            skLineSegment(sketch, "E10.33.3", {"start": v(-18.3, 0) * mm, "end": v(-18.3, -0.33) * mm});
            skLineSegment(sketch, "E10.33.4", {"start": v(-17.8, 0.5) * mm, "end": v(-18.3, 0.33) * mm});
            skLineSegment(sketch, "E10.33.5", {"start": v(-17.7, 0.5) * mm, "end": v(-17.8, 0.5) * mm});
            skLineSegment(sketch, "E10.34.0", {"start": v(-17.57, -2.18) * mm, "end": v(-17.66, -2.19) * mm});
            skLineSegment(sketch, "E10.34.1", {"start": v(-17.66, -2.19) * mm, "end": v(-18.19, -2.07) * mm});
            skLineSegment(sketch, "E10.34.2", {"start": v(-18.22, -1.74) * mm, "end": v(-18.25, -1.41) * mm});
            skLineSegment(sketch, "E10.34.3", {"start": v(-18.22, -1.74) * mm, "end": v(-18.19, -2.07) * mm});
            skLineSegment(sketch, "E10.34.4", {"start": v(-17.76, -1.2) * mm, "end": v(-18.25, -1.41) * mm});
            skLineSegment(sketch, "E10.34.5", {"start": v(-17.66, -1.18) * mm, "end": v(-17.76, -1.2) * mm});
            skLineSegment(sketch, "E10.35.0", {"start": v(-17.28, -3.84) * mm, "end": v(-17.38, -3.86) * mm});
            skLineSegment(sketch, "E10.35.1", {"start": v(-17.38, -3.86) * mm, "end": v(-17.9, -3.79) * mm});
            skLineSegment(sketch, "E10.35.2", {"start": v(-17.97, -3.46) * mm, "end": v(-18.03, -3.14) * mm});
            skLineSegment(sketch, "E10.35.3", {"start": v(-17.97, -3.46) * mm, "end": v(-17.9, -3.79) * mm});
            skLineSegment(sketch, "E10.35.4", {"start": v(-17.57, -2.88) * mm, "end": v(-18.03, -3.14) * mm});
            skLineSegment(sketch, "E10.35.5", {"start": v(-17.47, -2.86) * mm, "end": v(-17.57, -2.88) * mm});
            skLineSegment(sketch, "E10.36.0", {"start": v(-16.84, -5.46) * mm, "end": v(-16.93, -5.5) * mm});
            skLineSegment(sketch, "E10.36.1", {"start": v(-16.93, -5.5) * mm, "end": v(-17.47, -5.47) * mm});
            skLineSegment(sketch, "E10.36.2", {"start": v(-17.56, -5.16) * mm, "end": v(-17.65, -4.84) * mm});
            skLineSegment(sketch, "E10.36.3", {"start": v(-17.56, -5.16) * mm, "end": v(-17.47, -5.47) * mm});
            skLineSegment(sketch, "E10.36.4", {"start": v(-17.21, -4.53) * mm, "end": v(-17.65, -4.84) * mm});
            skLineSegment(sketch, "E10.36.5", {"start": v(-17.12, -4.5) * mm, "end": v(-17.21, -4.53) * mm});
            skLineSegment(sketch, "E10.37.0", {"start": v(-16.24, -7.04) * mm, "end": v(-16.33, -7.08) * mm});
            skLineSegment(sketch, "E10.37.1", {"start": v(-16.33, -7.08) * mm, "end": v(-16.87, -7.1) * mm});
            skLineSegment(sketch, "E10.37.2", {"start": v(-16.99, -6.8) * mm, "end": v(-17.11, -6.5) * mm});
            skLineSegment(sketch, "E10.37.3", {"start": v(-16.99, -6.8) * mm, "end": v(-16.87, -7.1) * mm});
            skLineSegment(sketch, "E10.37.4", {"start": v(-16.7, -6.15) * mm, "end": v(-17.11, -6.5) * mm});
            skLineSegment(sketch, "E10.37.5", {"start": v(-16.61, -6.11) * mm, "end": v(-16.7, -6.15) * mm});
            skLineSegment(sketch, "E10.38.0", {"start": v(-15.5, -8.55) * mm, "end": v(-15.59, -8.6) * mm});
            skLineSegment(sketch, "E10.38.1", {"start": v(-15.59, -8.6) * mm, "end": v(-16.11, -8.68) * mm});
            skLineSegment(sketch, "E10.38.2", {"start": v(-16.27, -8.39) * mm, "end": v(-16.42, -8.1) * mm});
            skLineSegment(sketch, "E10.38.3", {"start": v(-16.27, -8.39) * mm, "end": v(-16.11, -8.68) * mm});
            skLineSegment(sketch, "E10.38.4", {"start": v(-16.04, -7.7) * mm, "end": v(-16.42, -8.1) * mm});
            skLineSegment(sketch, "E10.38.5", {"start": v(-15.96, -7.66) * mm, "end": v(-16.04, -7.7) * mm});
            skLineSegment(sketch, "E10.39.0", {"start": v(-14.61, -9.99) * mm, "end": v(-14.7, -10.04) * mm});
            skLineSegment(sketch, "E10.39.1", {"start": v(-14.7, -10.04) * mm, "end": v(-15.22, -10.17) * mm});
            skLineSegment(sketch, "E10.39.2", {"start": v(-15.4, -9.9) * mm, "end": v(-15.57, -9.62) * mm});
            skLineSegment(sketch, "E10.39.3", {"start": v(-15.4, -9.9) * mm, "end": v(-15.22, -10.17) * mm});
            skLineSegment(sketch, "E10.39.4", {"start": v(-15.24, -9.2) * mm, "end": v(-15.57, -9.62) * mm});
            skLineSegment(sketch, "E10.39.5", {"start": v(-15.15, -9.14) * mm, "end": v(-15.24, -9.2) * mm});
            skLineSegment(sketch, "E10.40.0", {"start": v(-13.6, -11.33) * mm, "end": v(-13.68, -11.4) * mm});
            skLineSegment(sketch, "E10.40.1", {"start": v(-13.68, -11.4) * mm, "end": v(-14.18, -11.57) * mm});
            skLineSegment(sketch, "E10.40.2", {"start": v(-14.38, -11.31) * mm, "end": v(-14.59, -11.05) * mm});
            skLineSegment(sketch, "E10.40.3", {"start": v(-14.38, -11.31) * mm, "end": v(-14.18, -11.57) * mm});
            skLineSegment(sketch, "E10.40.4", {"start": v(-14.3, -10.6) * mm, "end": v(-14.59, -11.05) * mm});
            skLineSegment(sketch, "E10.40.5", {"start": v(-14.22, -10.54) * mm, "end": v(-14.3, -10.6) * mm});
            skLineSegment(sketch, "E10.41.0", {"start": v(-12.46, -12.57) * mm, "end": v(-12.53, -12.64) * mm});
            skLineSegment(sketch, "E10.41.1", {"start": v(-12.53, -12.64) * mm, "end": v(-13.02, -12.87) * mm});
            skLineSegment(sketch, "E10.41.2", {"start": v(-13.24, -12.63) * mm, "end": v(-13.47, -12.39) * mm});
            skLineSegment(sketch, "E10.41.3", {"start": v(-13.24, -12.63) * mm, "end": v(-13.02, -12.87) * mm});
            skLineSegment(sketch, "E10.41.4", {"start": v(-13.22, -11.92) * mm, "end": v(-13.47, -12.39) * mm});
            skLineSegment(sketch, "E10.41.5", {"start": v(-13.15, -11.85) * mm, "end": v(-13.22, -11.92) * mm});
            skLineSegment(sketch, "E10.42.0", {"start": v(-11.2, -13.7) * mm, "end": v(-11.27, -13.77) * mm});
            skLineSegment(sketch, "E10.42.1", {"start": v(-11.27, -13.77) * mm, "end": v(-11.73, -14.05) * mm});
            skLineSegment(sketch, "E10.42.2", {"start": v(-11.98, -13.83) * mm, "end": v(-12.23, -13.61) * mm});
            skLineSegment(sketch, "E10.42.3", {"start": v(-11.98, -13.83) * mm, "end": v(-11.73, -14.05) * mm});
            skLineSegment(sketch, "E10.42.4", {"start": v(-12.03, -13.12) * mm, "end": v(-12.23, -13.61) * mm});
            skLineSegment(sketch, "E10.42.5", {"start": v(-11.96, -13.04) * mm, "end": v(-12.03, -13.12) * mm});
            skLineSegment(sketch, "E10.43.0", {"start": v(-9.86, -14.7) * mm, "end": v(-9.91, -14.78) * mm});
            skLineSegment(sketch, "E10.43.1", {"start": v(-9.91, -14.78) * mm, "end": v(-10.35, -15.1) * mm});
            skLineSegment(sketch, "E10.43.2", {"start": v(-10.62, -14.9) * mm, "end": v(-10.88, -14.72) * mm});
            skLineSegment(sketch, "E10.43.3", {"start": v(-10.62, -14.9) * mm, "end": v(-10.35, -15.1) * mm});
            skLineSegment(sketch, "E10.43.4", {"start": v(-10.73, -14.2) * mm, "end": v(-10.88, -14.72) * mm});
            skLineSegment(sketch, "E10.43.5", {"start": v(-10.67, -14.12) * mm, "end": v(-10.73, -14.2) * mm});
            skLineSegment(sketch, "E10.44.0", {"start": v(-8.41, -15.57) * mm, "end": v(-8.46, -15.66) * mm});
            skLineSegment(sketch, "E10.44.1", {"start": v(-8.46, -15.66) * mm, "end": v(-8.86, -16.01) * mm});
            skLineSegment(sketch, "E10.44.2", {"start": v(-9.15, -15.85) * mm, "end": v(-9.44, -15.68) * mm});
            skLineSegment(sketch, "E10.44.3", {"start": v(-9.15, -15.85) * mm, "end": v(-8.86, -16.01) * mm});
            skLineSegment(sketch, "E10.44.4", {"start": v(-9.33, -15.16) * mm, "end": v(-9.44, -15.68) * mm});
            skLineSegment(sketch, "E10.44.5", {"start": v(-9.28, -15.07) * mm, "end": v(-9.33, -15.16) * mm});
            skLineSegment(sketch, "E10.45.0", {"start": v(-6.9, -16.3) * mm, "end": v(-6.94, -16.4) * mm});
            skLineSegment(sketch, "E10.45.1", {"start": v(-6.94, -16.4) * mm, "end": v(-7.3, -16.78) * mm});
            skLineSegment(sketch, "E10.45.2", {"start": v(-7.6, -16.65) * mm, "end": v(-7.9, -16.5) * mm});
            skLineSegment(sketch, "E10.45.3", {"start": v(-7.6, -16.65) * mm, "end": v(-7.3, -16.78) * mm});
            skLineSegment(sketch, "E10.45.4", {"start": v(-7.85, -15.98) * mm, "end": v(-7.9, -16.5) * mm});
            skLineSegment(sketch, "E10.45.5", {"start": v(-7.8, -15.89) * mm, "end": v(-7.85, -15.98) * mm});
            skLineSegment(sketch, "E10.46.0", {"start": v(-5.31, -16.88) * mm, "end": v(-5.35, -16.98) * mm});
            skLineSegment(sketch, "E10.46.1", {"start": v(-5.35, -16.98) * mm, "end": v(-5.67, -17.4) * mm});
            skLineSegment(sketch, "E10.46.2", {"start": v(-5.99, -17.3) * mm, "end": v(-6.3, -17.19) * mm});
            skLineSegment(sketch, "E10.46.3", {"start": v(-5.99, -17.3) * mm, "end": v(-5.67, -17.4) * mm});
            skLineSegment(sketch, "E10.46.4", {"start": v(-6.3, -16.65) * mm, "end": v(-6.3, -17.19) * mm});
            skLineSegment(sketch, "E10.46.5", {"start": v(-6.26, -16.56) * mm, "end": v(-6.3, -16.65) * mm});
            skLineSegment(sketch, "E10.47.0", {"start": v(-3.69, -17.31) * mm, "end": v(-3.7, -17.4) * mm});
            skLineSegment(sketch, "E10.47.1", {"start": v(-3.7, -17.4) * mm, "end": v(-4, -17.86) * mm});
            skLineSegment(sketch, "E10.47.2", {"start": v(-4.31, -17.78) * mm, "end": v(-4.64, -17.7) * mm});
            skLineSegment(sketch, "E10.47.3", {"start": v(-4.31, -17.78) * mm, "end": v(-4, -17.86) * mm});
            skLineSegment(sketch, "E10.47.4", {"start": v(-4.68, -17.17) * mm, "end": v(-4.64, -17.7) * mm});
            skLineSegment(sketch, "E10.47.5", {"start": v(-4.66, -17.08) * mm, "end": v(-4.68, -17.17) * mm});
            skLineSegment(sketch, "E10.48.0", {"start": v(-2.02, -17.58) * mm, "end": v(-2.04, -17.68) * mm});
            skLineSegment(sketch, "E10.48.1", {"start": v(-2.04, -17.68) * mm, "end": v(-2.28, -18.16) * mm});
            skLineSegment(sketch, "E10.48.2", {"start": v(-2.6, -18.11) * mm, "end": v(-2.93, -18.07) * mm});
            skLineSegment(sketch, "E10.48.3", {"start": v(-2.6, -18.11) * mm, "end": v(-2.28, -18.16) * mm});
            skLineSegment(sketch, "E10.48.4", {"start": v(-3.03, -17.54) * mm, "end": v(-2.93, -18.07) * mm});
            skLineSegment(sketch, "E10.48.5", {"start": v(-3.01, -17.44) * mm, "end": v(-3.03, -17.54) * mm});
            skLineSegment(sketch, "E10.49.0", {"start": v(-0.34, -17.7) * mm, "end": v(-0.35, -17.8) * mm});
            skLineSegment(sketch, "E10.49.1", {"start": v(-0.35, -17.8) * mm, "end": v(-0.54, -18.3) * mm});
            skLineSegment(sketch, "E10.49.2", {"start": v(-0.87, -18.28) * mm, "end": v(-1.2, -18.26) * mm});
            skLineSegment(sketch, "E10.49.3", {"start": v(-0.87, -18.28) * mm, "end": v(-0.54, -18.3) * mm});
            skLineSegment(sketch, "E10.49.4", {"start": v(-1.35, -17.75) * mm, "end": v(-1.2, -18.26) * mm});
            skLineSegment(sketch, "E10.49.5", {"start": v(-1.34, -17.65) * mm, "end": v(-1.35, -17.75) * mm});
            skLineSegment(sketch, "E10.50.0", {"start": v(1.34, -17.65) * mm, "end": v(1.35, -17.75) * mm});
            skLineSegment(sketch, "E10.50.1", {"start": v(1.35, -17.75) * mm, "end": v(1.2, -18.26) * mm});
            skLineSegment(sketch, "E10.50.2", {"start": v(0.87, -18.28) * mm, "end": v(0.54, -18.3) * mm});
            skLineSegment(sketch, "E10.50.3", {"start": v(0.87, -18.28) * mm, "end": v(1.2, -18.26) * mm});
            skLineSegment(sketch, "E10.50.4", {"start": v(0.35, -17.8) * mm, "end": v(0.54, -18.3) * mm});
            skLineSegment(sketch, "E10.50.5", {"start": v(0.34, -17.7) * mm, "end": v(0.35, -17.8) * mm});
            skLineSegment(sketch, "E10.51.0", {"start": v(3.01, -17.44) * mm, "end": v(3.03, -17.54) * mm});
            skLineSegment(sketch, "E10.51.1", {"start": v(3.03, -17.54) * mm, "end": v(2.93, -18.07) * mm});
            skLineSegment(sketch, "E10.51.2", {"start": v(2.6, -18.11) * mm, "end": v(2.28, -18.16) * mm});
            skLineSegment(sketch, "E10.51.3", {"start": v(2.6, -18.11) * mm, "end": v(2.93, -18.07) * mm});
            skLineSegment(sketch, "E10.51.4", {"start": v(2.04, -17.68) * mm, "end": v(2.28, -18.16) * mm});
            skLineSegment(sketch, "E10.51.5", {"start": v(2.02, -17.58) * mm, "end": v(2.04, -17.68) * mm});
            skLineSegment(sketch, "E10.52.0", {"start": v(4.66, -17.08) * mm, "end": v(4.68, -17.17) * mm});
            skLineSegment(sketch, "E10.52.1", {"start": v(4.68, -17.17) * mm, "end": v(4.64, -17.7) * mm});
            skLineSegment(sketch, "E10.52.2", {"start": v(4.31, -17.78) * mm, "end": v(4, -17.86) * mm});
            skLineSegment(sketch, "E10.52.3", {"start": v(4.31, -17.78) * mm, "end": v(4.64, -17.7) * mm});
            skLineSegment(sketch, "E10.52.4", {"start": v(3.7, -17.4) * mm, "end": v(4, -17.86) * mm});
            skLineSegment(sketch, "E10.52.5", {"start": v(3.69, -17.31) * mm, "end": v(3.7, -17.4) * mm});
            skLineSegment(sketch, "E10.53.0", {"start": v(6.26, -16.56) * mm, "end": v(6.3, -16.65) * mm});
            skLineSegment(sketch, "E10.53.1", {"start": v(6.3, -16.65) * mm, "end": v(6.3, -17.19) * mm});
            skLineSegment(sketch, "E10.53.2", {"start": v(5.99, -17.3) * mm, "end": v(5.67, -17.4) * mm});
            skLineSegment(sketch, "E10.53.3", {"start": v(5.99, -17.3) * mm, "end": v(6.3, -17.19) * mm});
            skLineSegment(sketch, "E10.53.4", {"start": v(5.35, -16.98) * mm, "end": v(5.67, -17.4) * mm});
            skLineSegment(sketch, "E10.53.5", {"start": v(5.31, -16.88) * mm, "end": v(5.35, -16.98) * mm});
            skLineSegment(sketch, "E10.54.0", {"start": v(7.8, -15.89) * mm, "end": v(7.85, -15.98) * mm});
            skLineSegment(sketch, "E10.54.1", {"start": v(7.85, -15.98) * mm, "end": v(7.9, -16.5) * mm});
            skLineSegment(sketch, "E10.54.2", {"start": v(7.6, -16.65) * mm, "end": v(7.3, -16.78) * mm});
            skLineSegment(sketch, "E10.54.3", {"start": v(7.6, -16.65) * mm, "end": v(7.9, -16.5) * mm});
            skLineSegment(sketch, "E10.54.4", {"start": v(6.94, -16.4) * mm, "end": v(7.3, -16.78) * mm});
            skLineSegment(sketch, "E10.54.5", {"start": v(6.9, -16.3) * mm, "end": v(6.94, -16.4) * mm});
            skLineSegment(sketch, "E10.55.0", {"start": v(9.28, -15.07) * mm, "end": v(9.33, -15.16) * mm});
            skLineSegment(sketch, "E10.55.1", {"start": v(9.33, -15.16) * mm, "end": v(9.44, -15.68) * mm});
            skLineSegment(sketch, "E10.55.2", {"start": v(9.15, -15.85) * mm, "end": v(8.86, -16.01) * mm});
            skLineSegment(sketch, "E10.55.3", {"start": v(9.15, -15.85) * mm, "end": v(9.44, -15.68) * mm});
            skLineSegment(sketch, "E10.55.4", {"start": v(8.46, -15.66) * mm, "end": v(8.86, -16.01) * mm});
            skLineSegment(sketch, "E10.55.5", {"start": v(8.41, -15.57) * mm, "end": v(8.46, -15.66) * mm});
            skLineSegment(sketch, "E10.56.0", {"start": v(10.67, -14.12) * mm, "end": v(10.73, -14.2) * mm});
            skLineSegment(sketch, "E10.56.1", {"start": v(10.73, -14.2) * mm, "end": v(10.88, -14.72) * mm});
            skLineSegment(sketch, "E10.56.2", {"start": v(10.62, -14.9) * mm, "end": v(10.35, -15.1) * mm});
            skLineSegment(sketch, "E10.56.3", {"start": v(10.62, -14.9) * mm, "end": v(10.88, -14.72) * mm});
            skLineSegment(sketch, "E10.56.4", {"start": v(9.91, -14.78) * mm, "end": v(10.35, -15.1) * mm});
            skLineSegment(sketch, "E10.56.5", {"start": v(9.86, -14.7) * mm, "end": v(9.91, -14.78) * mm});
            skLineSegment(sketch, "E10.57.0", {"start": v(11.96, -13.04) * mm, "end": v(12.03, -13.12) * mm});
            skLineSegment(sketch, "E10.57.1", {"start": v(12.03, -13.12) * mm, "end": v(12.23, -13.61) * mm});
            skLineSegment(sketch, "E10.57.2", {"start": v(11.98, -13.83) * mm, "end": v(11.73, -14.05) * mm});
            skLineSegment(sketch, "E10.57.3", {"start": v(11.98, -13.83) * mm, "end": v(12.23, -13.61) * mm});
            skLineSegment(sketch, "E10.57.4", {"start": v(11.27, -13.77) * mm, "end": v(11.73, -14.05) * mm});
            skLineSegment(sketch, "E10.57.5", {"start": v(11.2, -13.7) * mm, "end": v(11.27, -13.77) * mm});
            skLineSegment(sketch, "E10.58.0", {"start": v(13.15, -11.85) * mm, "end": v(13.22, -11.92) * mm});
            skLineSegment(sketch, "E10.58.1", {"start": v(13.22, -11.92) * mm, "end": v(13.47, -12.39) * mm});
            skLineSegment(sketch, "E10.58.2", {"start": v(13.24, -12.63) * mm, "end": v(13.02, -12.87) * mm});
            skLineSegment(sketch, "E10.58.3", {"start": v(13.24, -12.63) * mm, "end": v(13.47, -12.39) * mm});
            skLineSegment(sketch, "E10.58.4", {"start": v(12.53, -12.64) * mm, "end": v(13.02, -12.87) * mm});
            skLineSegment(sketch, "E10.58.5", {"start": v(12.46, -12.57) * mm, "end": v(12.53, -12.64) * mm});
            skLineSegment(sketch, "E10.59.0", {"start": v(14.22, -10.54) * mm, "end": v(14.3, -10.6) * mm});
            skLineSegment(sketch, "E10.59.1", {"start": v(14.3, -10.6) * mm, "end": v(14.59, -11.05) * mm});
            skLineSegment(sketch, "E10.59.2", {"start": v(14.38, -11.31) * mm, "end": v(14.18, -11.57) * mm});
            skLineSegment(sketch, "E10.59.3", {"start": v(14.38, -11.31) * mm, "end": v(14.59, -11.05) * mm});
            skLineSegment(sketch, "E10.59.4", {"start": v(13.68, -11.4) * mm, "end": v(14.18, -11.57) * mm});
            skLineSegment(sketch, "E10.59.5", {"start": v(13.6, -11.33) * mm, "end": v(13.68, -11.4) * mm});
            skLineSegment(sketch, "E10.60.0", {"start": v(15.15, -9.14) * mm, "end": v(15.24, -9.2) * mm});
            skLineSegment(sketch, "E10.60.1", {"start": v(15.24, -9.2) * mm, "end": v(15.57, -9.62) * mm});
            skLineSegment(sketch, "E10.60.2", {"start": v(15.4, -9.9) * mm, "end": v(15.22, -10.17) * mm});
            skLineSegment(sketch, "E10.60.3", {"start": v(15.4, -9.9) * mm, "end": v(15.57, -9.62) * mm});
            skLineSegment(sketch, "E10.60.4", {"start": v(14.7, -10.04) * mm, "end": v(15.22, -10.17) * mm});
            skLineSegment(sketch, "E10.60.5", {"start": v(14.61, -9.99) * mm, "end": v(14.7, -10.04) * mm});
            skLineSegment(sketch, "E10.61.0", {"start": v(15.96, -7.66) * mm, "end": v(16.04, -7.7) * mm});
            skLineSegment(sketch, "E10.61.1", {"start": v(16.04, -7.7) * mm, "end": v(16.42, -8.1) * mm});
            skLineSegment(sketch, "E10.61.2", {"start": v(16.27, -8.39) * mm, "end": v(16.11, -8.68) * mm});
            skLineSegment(sketch, "E10.61.3", {"start": v(16.27, -8.39) * mm, "end": v(16.42, -8.1) * mm});
            skLineSegment(sketch, "E10.61.4", {"start": v(15.59, -8.6) * mm, "end": v(16.11, -8.68) * mm});
            skLineSegment(sketch, "E10.61.5", {"start": v(15.5, -8.55) * mm, "end": v(15.59, -8.6) * mm});
            skLineSegment(sketch, "E10.62.0", {"start": v(16.61, -6.11) * mm, "end": v(16.7, -6.15) * mm});
            skLineSegment(sketch, "E10.62.1", {"start": v(16.7, -6.15) * mm, "end": v(17.11, -6.5) * mm});
            skLineSegment(sketch, "E10.62.2", {"start": v(16.99, -6.8) * mm, "end": v(16.87, -7.1) * mm});
            skLineSegment(sketch, "E10.62.3", {"start": v(16.99, -6.8) * mm, "end": v(17.11, -6.5) * mm});
            skLineSegment(sketch, "E10.62.4", {"start": v(16.33, -7.08) * mm, "end": v(16.87, -7.1) * mm});
            skLineSegment(sketch, "E10.62.5", {"start": v(16.24, -7.04) * mm, "end": v(16.33, -7.08) * mm});
            skLineSegment(sketch, "E10.63.0", {"start": v(17.12, -4.5) * mm, "end": v(17.21, -4.53) * mm});
            skLineSegment(sketch, "E10.63.1", {"start": v(17.21, -4.53) * mm, "end": v(17.65, -4.84) * mm});
            skLineSegment(sketch, "E10.63.2", {"start": v(17.56, -5.16) * mm, "end": v(17.47, -5.47) * mm});
            skLineSegment(sketch, "E10.63.3", {"start": v(17.56, -5.16) * mm, "end": v(17.65, -4.84) * mm});
            skLineSegment(sketch, "E10.63.4", {"start": v(16.93, -5.5) * mm, "end": v(17.47, -5.47) * mm});
            skLineSegment(sketch, "E10.63.5", {"start": v(16.84, -5.46) * mm, "end": v(16.93, -5.5) * mm});
            skLineSegment(sketch, "E10.64.0", {"start": v(17.47, -2.86) * mm, "end": v(17.57, -2.88) * mm});
            skLineSegment(sketch, "E10.64.1", {"start": v(17.57, -2.88) * mm, "end": v(18.03, -3.14) * mm});
            skLineSegment(sketch, "E10.64.2", {"start": v(17.97, -3.46) * mm, "end": v(17.9, -3.79) * mm});
            skLineSegment(sketch, "E10.64.3", {"start": v(17.97, -3.46) * mm, "end": v(18.03, -3.14) * mm});
            skLineSegment(sketch, "E10.64.4", {"start": v(17.38, -3.86) * mm, "end": v(17.9, -3.79) * mm});
            skLineSegment(sketch, "E10.64.5", {"start": v(17.28, -3.84) * mm, "end": v(17.38, -3.86) * mm});
            skLineSegment(sketch, "E10.65.0", {"start": v(17.66, -1.18) * mm, "end": v(17.76, -1.2) * mm});
            skLineSegment(sketch, "E10.65.1", {"start": v(17.76, -1.2) * mm, "end": v(18.25, -1.41) * mm});
            skLineSegment(sketch, "E10.65.2", {"start": v(18.22, -1.74) * mm, "end": v(18.19, -2.07) * mm});
            skLineSegment(sketch, "E10.65.3", {"start": v(18.22, -1.74) * mm, "end": v(18.25, -1.41) * mm});
            skLineSegment(sketch, "E10.65.4", {"start": v(17.66, -2.19) * mm, "end": v(18.19, -2.07) * mm});
            skLineSegment(sketch, "E10.65.5", {"start": v(17.57, -2.18) * mm, "end": v(17.66, -2.19) * mm});
            skSolve(sketch);
        }
        {
            var Q0;
            Q0=qSketchRegion(id+"F0",true);
            extrude(context, id + "F1", {"entities" : qUnion([Q0]), "depth" : 10 * mm, "offsetDistance" : 25.4 * mm});
        }
        {
            var Q0;
            Q0=makeQuery(id+"F1.opExtrude","CAP_FACE",FACE,{"disambiguationData":[OSD([sQuery(id+"F0.wireOp",EDGE,"E0"),sQuery(id+"F0.wireOp",EDGE,"E3"),sQuery(id+"F0.wireOp",EDGE,"E4"),sQuery(id+"F0.wireOp",EDGE,"E5"),sQuery(id+"F0.wireOp",EDGE,"E6.MirrorCS"),sQuery(id+"F0.wireOp",EDGE,"E7.MirrorCS"),sQuery(id+"F0.wireOp",EDGE,"E8.MirrorCS"),sQuery(id+"F0.wireOp",EDGE,"E10.1.0"),sQuery(id+"F0.wireOp",EDGE,"E10.1.1"),sQuery(id+"F0.wireOp",EDGE,"E10.1.2"),sQuery(id+"F0.wireOp",EDGE,"E10.1.3"),sQuery(id+"F0.wireOp",EDGE,"E10.1.4"),sQuery(id+"F0.wireOp",EDGE,"E10.1.5"),sQuery(id+"F0.wireOp",EDGE,"E10.2.0"),sQuery(id+"F0.wireOp",EDGE,"E10.2.1"),sQuery(id+"F0.wireOp",EDGE,"E10.2.2"),sQuery(id+"F0.wireOp",EDGE,"E10.2.3"),sQuery(id+"F0.wireOp",EDGE,"E10.2.4"),sQuery(id+"F0.wireOp",EDGE,"E10.2.5"),sQuery(id+"F0.wireOp",EDGE,"E10.3.0"),sQuery(id+"F0.wireOp",EDGE,"E10.3.1"),sQuery(id+"F0.wireOp",EDGE,"E10.3.2"),sQuery(id+"F0.wireOp",EDGE,"E10.3.3"),sQuery(id+"F0.wireOp",EDGE,"E10.3.4"),sQuery(id+"F0.wireOp",EDGE,"E10.3.5"),sQuery(id+"F0.wireOp",EDGE,"E10.4.0"),sQuery(id+"F0.wireOp",EDGE,"E10.4.1"),sQuery(id+"F0.wireOp",EDGE,"E10.4.2"),sQuery(id+"F0.wireOp",EDGE,"E10.4.3"),sQuery(id+"F0.wireOp",EDGE,"E10.4.4"),sQuery(id+"F0.wireOp",EDGE,"E10.4.5"),sQuery(id+"F0.wireOp",EDGE,"E10.5.0"),sQuery(id+"F0.wireOp",EDGE,"E10.5.1"),sQuery(id+"F0.wireOp",EDGE,"E10.5.2"),sQuery(id+"F0.wireOp",EDGE,"E10.5.3"),sQuery(id+"F0.wireOp",EDGE,"E10.5.4"),sQuery(id+"F0.wireOp",EDGE,"E10.5.5"),sQuery(id+"F0.wireOp",EDGE,"E10.6.0"),sQuery(id+"F0.wireOp",EDGE,"E10.6.1"),sQuery(id+"F0.wireOp",EDGE,"E10.6.2"),sQuery(id+"F0.wireOp",EDGE,"E10.6.3"),sQuery(id+"F0.wireOp",EDGE,"E10.6.4"),sQuery(id+"F0.wireOp",EDGE,"E10.6.5"),sQuery(id+"F0.wireOp",EDGE,"E10.7.0"),sQuery(id+"F0.wireOp",EDGE,"E10.7.1"),sQuery(id+"F0.wireOp",EDGE,"E10.7.2"),sQuery(id+"F0.wireOp",EDGE,"E10.7.3"),sQuery(id+"F0.wireOp",EDGE,"E10.7.4"),sQuery(id+"F0.wireOp",EDGE,"E10.7.5"),sQuery(id+"F0.wireOp",EDGE,"E10.8.0"),sQuery(id+"F0.wireOp",EDGE,"E10.8.1"),sQuery(id+"F0.wireOp",EDGE,"E10.8.2"),sQuery(id+"F0.wireOp",EDGE,"E10.8.3"),sQuery(id+"F0.wireOp",EDGE,"E10.8.4"),sQuery(id+"F0.wireOp",EDGE,"E10.8.5"),sQuery(id+"F0.wireOp",EDGE,"E10.9.0"),sQuery(id+"F0.wireOp",EDGE,"E10.9.1"),sQuery(id+"F0.wireOp",EDGE,"E10.9.2"),sQuery(id+"F0.wireOp",EDGE,"E10.9.3"),sQuery(id+"F0.wireOp",EDGE,"E10.9.4"),sQuery(id+"F0.wireOp",EDGE,"E10.9.5"),sQuery(id+"F0.wireOp",EDGE,"E10.10.0"),sQuery(id+"F0.wireOp",EDGE,"E10.10.1"),sQuery(id+"F0.wireOp",EDGE,"E10.10.2"),sQuery(id+"F0.wireOp",EDGE,"E10.10.3"),sQuery(id+"F0.wireOp",EDGE,"E10.10.4"),sQuery(id+"F0.wireOp",EDGE,"E10.10.5"),sQuery(id+"F0.wireOp",EDGE,"E10.11.0"),sQuery(id+"F0.wireOp",EDGE,"E10.11.1"),sQuery(id+"F0.wireOp",EDGE,"E10.11.2"),sQuery(id+"F0.wireOp",EDGE,"E10.11.3"),sQuery(id+"F0.wireOp",EDGE,"E10.11.4"),sQuery(id+"F0.wireOp",EDGE,"E10.11.5"),sQuery(id+"F0.wireOp",EDGE,"E10.12.0"),sQuery(id+"F0.wireOp",EDGE,"E10.12.1"),sQuery(id+"F0.wireOp",EDGE,"E10.12.2"),sQuery(id+"F0.wireOp",EDGE,"E10.12.3"),sQuery(id+"F0.wireOp",EDGE,"E10.12.4"),sQuery(id+"F0.wireOp",EDGE,"E10.12.5"),sQuery(id+"F0.wireOp",EDGE,"E10.13.0"),sQuery(id+"F0.wireOp",EDGE,"E10.13.1"),sQuery(id+"F0.wireOp",EDGE,"E10.13.2"),sQuery(id+"F0.wireOp",EDGE,"E10.13.3"),sQuery(id+"F0.wireOp",EDGE,"E10.13.4"),sQuery(id+"F0.wireOp",EDGE,"E10.13.5"),sQuery(id+"F0.wireOp",EDGE,"E10.14.0"),sQuery(id+"F0.wireOp",EDGE,"E10.14.1"),sQuery(id+"F0.wireOp",EDGE,"E10.14.2"),sQuery(id+"F0.wireOp",EDGE,"E10.14.3"),sQuery(id+"F0.wireOp",EDGE,"E10.14.4"),sQuery(id+"F0.wireOp",EDGE,"E10.14.5"),sQuery(id+"F0.wireOp",EDGE,"E10.15.0"),sQuery(id+"F0.wireOp",EDGE,"E10.15.1"),sQuery(id+"F0.wireOp",EDGE,"E10.15.2"),sQuery(id+"F0.wireOp",EDGE,"E10.15.3"),sQuery(id+"F0.wireOp",EDGE,"E10.15.4"),sQuery(id+"F0.wireOp",EDGE,"E10.15.5"),sQuery(id+"F0.wireOp",EDGE,"E10.16.0"),sQuery(id+"F0.wireOp",EDGE,"E10.16.1"),sQuery(id+"F0.wireOp",EDGE,"E10.16.2"),sQuery(id+"F0.wireOp",EDGE,"E10.16.3"),sQuery(id+"F0.wireOp",EDGE,"E10.16.4"),sQuery(id+"F0.wireOp",EDGE,"E10.16.5"),sQuery(id+"F0.wireOp",EDGE,"E10.17.0"),sQuery(id+"F0.wireOp",EDGE,"E10.17.1"),sQuery(id+"F0.wireOp",EDGE,"E10.17.2"),sQuery(id+"F0.wireOp",EDGE,"E10.17.3"),sQuery(id+"F0.wireOp",EDGE,"E10.17.4"),sQuery(id+"F0.wireOp",EDGE,"E10.17.5"),sQuery(id+"F0.wireOp",EDGE,"E10.18.0"),sQuery(id+"F0.wireOp",EDGE,"E10.18.1"),sQuery(id+"F0.wireOp",EDGE,"E10.18.2"),sQuery(id+"F0.wireOp",EDGE,"E10.18.3"),sQuery(id+"F0.wireOp",EDGE,"E10.18.4"),sQuery(id+"F0.wireOp",EDGE,"E10.18.5"),sQuery(id+"F0.wireOp",EDGE,"E10.19.0"),sQuery(id+"F0.wireOp",EDGE,"E10.19.1"),sQuery(id+"F0.wireOp",EDGE,"E10.19.2"),sQuery(id+"F0.wireOp",EDGE,"E10.19.3"),sQuery(id+"F0.wireOp",EDGE,"E10.19.4"),sQuery(id+"F0.wireOp",EDGE,"E10.19.5"),sQuery(id+"F0.wireOp",EDGE,"E10.20.0"),sQuery(id+"F0.wireOp",EDGE,"E10.20.1"),sQuery(id+"F0.wireOp",EDGE,"E10.20.2"),sQuery(id+"F0.wireOp",EDGE,"E10.20.3"),sQuery(id+"F0.wireOp",EDGE,"E10.20.4"),sQuery(id+"F0.wireOp",EDGE,"E10.20.5"),sQuery(id+"F0.wireOp",EDGE,"E10.21.0"),sQuery(id+"F0.wireOp",EDGE,"E10.21.1"),sQuery(id+"F0.wireOp",EDGE,"E10.21.2"),sQuery(id+"F0.wireOp",EDGE,"E10.21.3"),sQuery(id+"F0.wireOp",EDGE,"E10.21.4"),sQuery(id+"F0.wireOp",EDGE,"E10.21.5"),sQuery(id+"F0.wireOp",EDGE,"E10.22.0"),sQuery(id+"F0.wireOp",EDGE,"E10.22.1"),sQuery(id+"F0.wireOp",EDGE,"E10.22.2"),sQuery(id+"F0.wireOp",EDGE,"E10.22.3"),sQuery(id+"F0.wireOp",EDGE,"E10.22.4"),sQuery(id+"F0.wireOp",EDGE,"E10.22.5"),sQuery(id+"F0.wireOp",EDGE,"E10.23.0"),sQuery(id+"F0.wireOp",EDGE,"E10.23.1"),sQuery(id+"F0.wireOp",EDGE,"E10.23.2"),sQuery(id+"F0.wireOp",EDGE,"E10.23.3"),sQuery(id+"F0.wireOp",EDGE,"E10.23.4"),sQuery(id+"F0.wireOp",EDGE,"E10.23.5"),sQuery(id+"F0.wireOp",EDGE,"E10.24.0"),sQuery(id+"F0.wireOp",EDGE,"E10.24.1"),sQuery(id+"F0.wireOp",EDGE,"E10.24.2"),sQuery(id+"F0.wireOp",EDGE,"E10.24.3"),sQuery(id+"F0.wireOp",EDGE,"E10.24.4"),sQuery(id+"F0.wireOp",EDGE,"E10.24.5"),sQuery(id+"F0.wireOp",EDGE,"E10.25.0"),sQuery(id+"F0.wireOp",EDGE,"E10.25.1"),sQuery(id+"F0.wireOp",EDGE,"E10.25.2"),sQuery(id+"F0.wireOp",EDGE,"E10.25.3"),sQuery(id+"F0.wireOp",EDGE,"E10.25.4"),sQuery(id+"F0.wireOp",EDGE,"E10.25.5"),sQuery(id+"F0.wireOp",EDGE,"E10.26.0"),sQuery(id+"F0.wireOp",EDGE,"E10.26.1"),sQuery(id+"F0.wireOp",EDGE,"E10.26.2"),sQuery(id+"F0.wireOp",EDGE,"E10.26.3"),sQuery(id+"F0.wireOp",EDGE,"E10.26.4"),sQuery(id+"F0.wireOp",EDGE,"E10.26.5"),sQuery(id+"F0.wireOp",EDGE,"E10.27.0"),sQuery(id+"F0.wireOp",EDGE,"E10.27.1"),sQuery(id+"F0.wireOp",EDGE,"E10.27.2"),sQuery(id+"F0.wireOp",EDGE,"E10.27.3"),sQuery(id+"F0.wireOp",EDGE,"E10.27.4"),sQuery(id+"F0.wireOp",EDGE,"E10.27.5"),sQuery(id+"F0.wireOp",EDGE,"E10.28.0"),sQuery(id+"F0.wireOp",EDGE,"E10.28.1"),sQuery(id+"F0.wireOp",EDGE,"E10.28.2"),sQuery(id+"F0.wireOp",EDGE,"E10.28.3"),sQuery(id+"F0.wireOp",EDGE,"E10.28.4"),sQuery(id+"F0.wireOp",EDGE,"E10.28.5"),sQuery(id+"F0.wireOp",EDGE,"E10.29.0"),sQuery(id+"F0.wireOp",EDGE,"E10.29.1"),sQuery(id+"F0.wireOp",EDGE,"E10.29.2"),sQuery(id+"F0.wireOp",EDGE,"E10.29.3"),sQuery(id+"F0.wireOp",EDGE,"E10.29.4"),sQuery(id+"F0.wireOp",EDGE,"E10.29.5"),sQuery(id+"F0.wireOp",EDGE,"E10.30.0"),sQuery(id+"F0.wireOp",EDGE,"E10.30.1"),sQuery(id+"F0.wireOp",EDGE,"E10.30.2"),sQuery(id+"F0.wireOp",EDGE,"E10.30.3"),sQuery(id+"F0.wireOp",EDGE,"E10.30.4"),sQuery(id+"F0.wireOp",EDGE,"E10.30.5"),sQuery(id+"F0.wireOp",EDGE,"E10.31.0"),sQuery(id+"F0.wireOp",EDGE,"E10.31.1"),sQuery(id+"F0.wireOp",EDGE,"E10.31.2"),sQuery(id+"F0.wireOp",EDGE,"E10.31.3"),sQuery(id+"F0.wireOp",EDGE,"E10.31.4"),sQuery(id+"F0.wireOp",EDGE,"E10.31.5"),sQuery(id+"F0.wireOp",EDGE,"E10.32.0"),sQuery(id+"F0.wireOp",EDGE,"E10.32.1"),sQuery(id+"F0.wireOp",EDGE,"E10.32.2"),sQuery(id+"F0.wireOp",EDGE,"E10.32.3"),sQuery(id+"F0.wireOp",EDGE,"E10.32.4"),sQuery(id+"F0.wireOp",EDGE,"E10.32.5"),sQuery(id+"F0.wireOp",EDGE,"E10.33.0"),sQuery(id+"F0.wireOp",EDGE,"E10.33.1"),sQuery(id+"F0.wireOp",EDGE,"E10.33.2"),sQuery(id+"F0.wireOp",EDGE,"E10.33.3"),sQuery(id+"F0.wireOp",EDGE,"E10.33.4"),sQuery(id+"F0.wireOp",EDGE,"E10.33.5"),sQuery(id+"F0.wireOp",EDGE,"E10.34.0"),sQuery(id+"F0.wireOp",EDGE,"E10.34.1"),sQuery(id+"F0.wireOp",EDGE,"E10.34.2"),sQuery(id+"F0.wireOp",EDGE,"E10.34.3"),sQuery(id+"F0.wireOp",EDGE,"E10.34.4"),sQuery(id+"F0.wireOp",EDGE,"E10.34.5"),sQuery(id+"F0.wireOp",EDGE,"E10.35.0"),sQuery(id+"F0.wireOp",EDGE,"E10.35.1"),sQuery(id+"F0.wireOp",EDGE,"E10.35.2"),sQuery(id+"F0.wireOp",EDGE,"E10.35.3"),sQuery(id+"F0.wireOp",EDGE,"E10.35.4"),sQuery(id+"F0.wireOp",EDGE,"E10.35.5"),sQuery(id+"F0.wireOp",EDGE,"E10.36.0"),sQuery(id+"F0.wireOp",EDGE,"E10.36.1"),sQuery(id+"F0.wireOp",EDGE,"E10.36.2"),sQuery(id+"F0.wireOp",EDGE,"E10.36.3"),sQuery(id+"F0.wireOp",EDGE,"E10.36.4"),sQuery(id+"F0.wireOp",EDGE,"E10.36.5"),sQuery(id+"F0.wireOp",EDGE,"E10.37.0"),sQuery(id+"F0.wireOp",EDGE,"E10.37.1"),sQuery(id+"F0.wireOp",EDGE,"E10.37.2"),sQuery(id+"F0.wireOp",EDGE,"E10.37.3"),sQuery(id+"F0.wireOp",EDGE,"E10.37.4"),sQuery(id+"F0.wireOp",EDGE,"E10.37.5"),sQuery(id+"F0.wireOp",EDGE,"E10.38.0"),sQuery(id+"F0.wireOp",EDGE,"E10.38.1"),sQuery(id+"F0.wireOp",EDGE,"E10.38.2"),sQuery(id+"F0.wireOp",EDGE,"E10.38.3"),sQuery(id+"F0.wireOp",EDGE,"E10.38.4"),sQuery(id+"F0.wireOp",EDGE,"E10.38.5"),sQuery(id+"F0.wireOp",EDGE,"E10.39.0"),sQuery(id+"F0.wireOp",EDGE,"E10.39.1"),sQuery(id+"F0.wireOp",EDGE,"E10.39.2"),sQuery(id+"F0.wireOp",EDGE,"E10.39.3"),sQuery(id+"F0.wireOp",EDGE,"E10.39.4"),sQuery(id+"F0.wireOp",EDGE,"E10.39.5"),sQuery(id+"F0.wireOp",EDGE,"E10.40.0"),sQuery(id+"F0.wireOp",EDGE,"E10.40.1"),sQuery(id+"F0.wireOp",EDGE,"E10.40.2"),sQuery(id+"F0.wireOp",EDGE,"E10.40.3"),sQuery(id+"F0.wireOp",EDGE,"E10.40.4"),sQuery(id+"F0.wireOp",EDGE,"E10.40.5"),sQuery(id+"F0.wireOp",EDGE,"E10.41.0"),sQuery(id+"F0.wireOp",EDGE,"E10.41.1"),sQuery(id+"F0.wireOp",EDGE,"E10.41.2"),sQuery(id+"F0.wireOp",EDGE,"E10.41.3"),sQuery(id+"F0.wireOp",EDGE,"E10.41.4"),sQuery(id+"F0.wireOp",EDGE,"E10.41.5"),sQuery(id+"F0.wireOp",EDGE,"E10.42.0"),sQuery(id+"F0.wireOp",EDGE,"E10.42.1"),sQuery(id+"F0.wireOp",EDGE,"E10.42.2"),sQuery(id+"F0.wireOp",EDGE,"E10.42.3"),sQuery(id+"F0.wireOp",EDGE,"E10.42.4"),sQuery(id+"F0.wireOp",EDGE,"E10.42.5"),sQuery(id+"F0.wireOp",EDGE,"E10.43.0"),sQuery(id+"F0.wireOp",EDGE,"E10.43.1"),sQuery(id+"F0.wireOp",EDGE,"E10.43.2"),sQuery(id+"F0.wireOp",EDGE,"E10.43.3"),sQuery(id+"F0.wireOp",EDGE,"E10.43.4"),sQuery(id+"F0.wireOp",EDGE,"E10.43.5"),sQuery(id+"F0.wireOp",EDGE,"E10.44.0"),sQuery(id+"F0.wireOp",EDGE,"E10.44.1"),sQuery(id+"F0.wireOp",EDGE,"E10.44.2"),sQuery(id+"F0.wireOp",EDGE,"E10.44.3"),sQuery(id+"F0.wireOp",EDGE,"E10.44.4"),sQuery(id+"F0.wireOp",EDGE,"E10.44.5"),sQuery(id+"F0.wireOp",EDGE,"E10.45.0"),sQuery(id+"F0.wireOp",EDGE,"E10.45.1"),sQuery(id+"F0.wireOp",EDGE,"E10.45.2"),sQuery(id+"F0.wireOp",EDGE,"E10.45.3"),sQuery(id+"F0.wireOp",EDGE,"E10.45.4"),sQuery(id+"F0.wireOp",EDGE,"E10.45.5"),sQuery(id+"F0.wireOp",EDGE,"E10.46.0"),sQuery(id+"F0.wireOp",EDGE,"E10.46.1"),sQuery(id+"F0.wireOp",EDGE,"E10.46.2"),sQuery(id+"F0.wireOp",EDGE,"E10.46.3"),sQuery(id+"F0.wireOp",EDGE,"E10.46.4"),sQuery(id+"F0.wireOp",EDGE,"E10.46.5"),sQuery(id+"F0.wireOp",EDGE,"E10.47.0"),sQuery(id+"F0.wireOp",EDGE,"E10.47.1"),sQuery(id+"F0.wireOp",EDGE,"E10.47.2"),sQuery(id+"F0.wireOp",EDGE,"E10.47.3"),sQuery(id+"F0.wireOp",EDGE,"E10.47.4"),sQuery(id+"F0.wireOp",EDGE,"E10.47.5"),sQuery(id+"F0.wireOp",EDGE,"E10.48.0"),sQuery(id+"F0.wireOp",EDGE,"E10.48.1"),sQuery(id+"F0.wireOp",EDGE,"E10.48.2"),sQuery(id+"F0.wireOp",EDGE,"E10.48.3"),sQuery(id+"F0.wireOp",EDGE,"E10.48.4"),sQuery(id+"F0.wireOp",EDGE,"E10.48.5"),sQuery(id+"F0.wireOp",EDGE,"E10.49.0"),sQuery(id+"F0.wireOp",EDGE,"E10.49.1"),sQuery(id+"F0.wireOp",EDGE,"E10.49.2"),sQuery(id+"F0.wireOp",EDGE,"E10.49.3"),sQuery(id+"F0.wireOp",EDGE,"E10.49.4"),sQuery(id+"F0.wireOp",EDGE,"E10.49.5"),sQuery(id+"F0.wireOp",EDGE,"E10.50.0"),sQuery(id+"F0.wireOp",EDGE,"E10.50.1"),sQuery(id+"F0.wireOp",EDGE,"E10.50.2"),sQuery(id+"F0.wireOp",EDGE,"E10.50.3"),sQuery(id+"F0.wireOp",EDGE,"E10.50.4"),sQuery(id+"F0.wireOp",EDGE,"E10.50.5"),sQuery(id+"F0.wireOp",EDGE,"E10.51.0"),sQuery(id+"F0.wireOp",EDGE,"E10.51.1"),sQuery(id+"F0.wireOp",EDGE,"E10.51.2"),sQuery(id+"F0.wireOp",EDGE,"E10.51.3"),sQuery(id+"F0.wireOp",EDGE,"E10.51.4"),sQuery(id+"F0.wireOp",EDGE,"E10.51.5"),sQuery(id+"F0.wireOp",EDGE,"E10.52.0"),sQuery(id+"F0.wireOp",EDGE,"E10.52.1"),sQuery(id+"F0.wireOp",EDGE,"E10.52.2"),sQuery(id+"F0.wireOp",EDGE,"E10.52.3"),sQuery(id+"F0.wireOp",EDGE,"E10.52.4"),sQuery(id+"F0.wireOp",EDGE,"E10.52.5"),sQuery(id+"F0.wireOp",EDGE,"E10.53.0"),sQuery(id+"F0.wireOp",EDGE,"E10.53.1"),sQuery(id+"F0.wireOp",EDGE,"E10.53.2"),sQuery(id+"F0.wireOp",EDGE,"E10.53.3"),sQuery(id+"F0.wireOp",EDGE,"E10.53.4"),sQuery(id+"F0.wireOp",EDGE,"E10.53.5"),sQuery(id+"F0.wireOp",EDGE,"E10.54.0"),sQuery(id+"F0.wireOp",EDGE,"E10.54.1"),sQuery(id+"F0.wireOp",EDGE,"E10.54.2"),sQuery(id+"F0.wireOp",EDGE,"E10.54.3"),sQuery(id+"F0.wireOp",EDGE,"E10.54.4"),sQuery(id+"F0.wireOp",EDGE,"E10.54.5"),sQuery(id+"F0.wireOp",EDGE,"E10.55.0"),sQuery(id+"F0.wireOp",EDGE,"E10.55.1"),sQuery(id+"F0.wireOp",EDGE,"E10.55.2"),sQuery(id+"F0.wireOp",EDGE,"E10.55.3"),sQuery(id+"F0.wireOp",EDGE,"E10.55.4"),sQuery(id+"F0.wireOp",EDGE,"E10.55.5"),sQuery(id+"F0.wireOp",EDGE,"E10.56.0"),sQuery(id+"F0.wireOp",EDGE,"E10.56.1"),sQuery(id+"F0.wireOp",EDGE,"E10.56.2"),sQuery(id+"F0.wireOp",EDGE,"E10.56.3"),sQuery(id+"F0.wireOp",EDGE,"E10.56.4"),sQuery(id+"F0.wireOp",EDGE,"E10.56.5"),sQuery(id+"F0.wireOp",EDGE,"E10.57.0"),sQuery(id+"F0.wireOp",EDGE,"E10.57.1"),sQuery(id+"F0.wireOp",EDGE,"E10.57.2"),sQuery(id+"F0.wireOp",EDGE,"E10.57.3"),sQuery(id+"F0.wireOp",EDGE,"E10.57.4"),sQuery(id+"F0.wireOp",EDGE,"E10.57.5"),sQuery(id+"F0.wireOp",EDGE,"E10.58.0"),sQuery(id+"F0.wireOp",EDGE,"E10.58.1"),sQuery(id+"F0.wireOp",EDGE,"E10.58.2"),sQuery(id+"F0.wireOp",EDGE,"E10.58.3"),sQuery(id+"F0.wireOp",EDGE,"E10.58.4"),sQuery(id+"F0.wireOp",EDGE,"E10.58.5"),sQuery(id+"F0.wireOp",EDGE,"E10.59.0"),sQuery(id+"F0.wireOp",EDGE,"E10.59.1"),sQuery(id+"F0.wireOp",EDGE,"E10.59.2"),sQuery(id+"F0.wireOp",EDGE,"E10.59.3"),sQuery(id+"F0.wireOp",EDGE,"E10.59.4"),sQuery(id+"F0.wireOp",EDGE,"E10.59.5"),sQuery(id+"F0.wireOp",EDGE,"E10.60.0"),sQuery(id+"F0.wireOp",EDGE,"E10.60.1"),sQuery(id+"F0.wireOp",EDGE,"E10.60.2"),sQuery(id+"F0.wireOp",EDGE,"E10.60.3"),sQuery(id+"F0.wireOp",EDGE,"E10.60.4"),sQuery(id+"F0.wireOp",EDGE,"E10.60.5"),sQuery(id+"F0.wireOp",EDGE,"E10.61.0"),sQuery(id+"F0.wireOp",EDGE,"E10.61.1"),sQuery(id+"F0.wireOp",EDGE,"E10.61.2"),sQuery(id+"F0.wireOp",EDGE,"E10.61.3"),sQuery(id+"F0.wireOp",EDGE,"E10.61.4"),sQuery(id+"F0.wireOp",EDGE,"E10.61.5"),sQuery(id+"F0.wireOp",EDGE,"E10.62.0"),sQuery(id+"F0.wireOp",EDGE,"E10.62.1"),sQuery(id+"F0.wireOp",EDGE,"E10.62.2"),sQuery(id+"F0.wireOp",EDGE,"E10.62.3"),sQuery(id+"F0.wireOp",EDGE,"E10.62.4"),sQuery(id+"F0.wireOp",EDGE,"E10.62.5"),sQuery(id+"F0.wireOp",EDGE,"E10.63.0"),sQuery(id+"F0.wireOp",EDGE,"E10.63.1"),sQuery(id+"F0.wireOp",EDGE,"E10.63.2"),sQuery(id+"F0.wireOp",EDGE,"E10.63.3"),sQuery(id+"F0.wireOp",EDGE,"E10.63.4"),sQuery(id+"F0.wireOp",EDGE,"E10.63.5"),sQuery(id+"F0.wireOp",EDGE,"E10.64.0"),sQuery(id+"F0.wireOp",EDGE,"E10.64.1"),sQuery(id+"F0.wireOp",EDGE,"E10.64.2"),sQuery(id+"F0.wireOp",EDGE,"E10.64.3"),sQuery(id+"F0.wireOp",EDGE,"E10.64.4"),sQuery(id+"F0.wireOp",EDGE,"E10.64.5"),sQuery(id+"F0.wireOp",EDGE,"E10.65.0"),sQuery(id+"F0.wireOp",EDGE,"E10.65.1"),sQuery(id+"F0.wireOp",EDGE,"E10.65.2"),sQuery(id+"F0.wireOp",EDGE,"E10.65.3"),sQuery(id+"F0.wireOp",EDGE,"E10.65.4"),sQuery(id+"F0.wireOp",EDGE,"E10.65.5")])],"isStart":false});
            var sketch = newSketch(context, id + "F2", { "sketchPlane" : qUnion([Q0])});
            skCircle(sketch, "E11", {"center": v(0, 0) * mm, "radius": 2 * mm});
            skSolve(sketch);
        }
        {
            var Q0;
            Q0=qSketchRegion(id+"F2",true);
            extrude(context, id + "F3", {"entities" : qUnion([Q0]), "operationType" : NewBodyOperationType.REMOVE, "oppositeDirection" : true, "depth" : 25.4 * mm, "offsetDistance" : 25.4 * mm});
        }
    });
